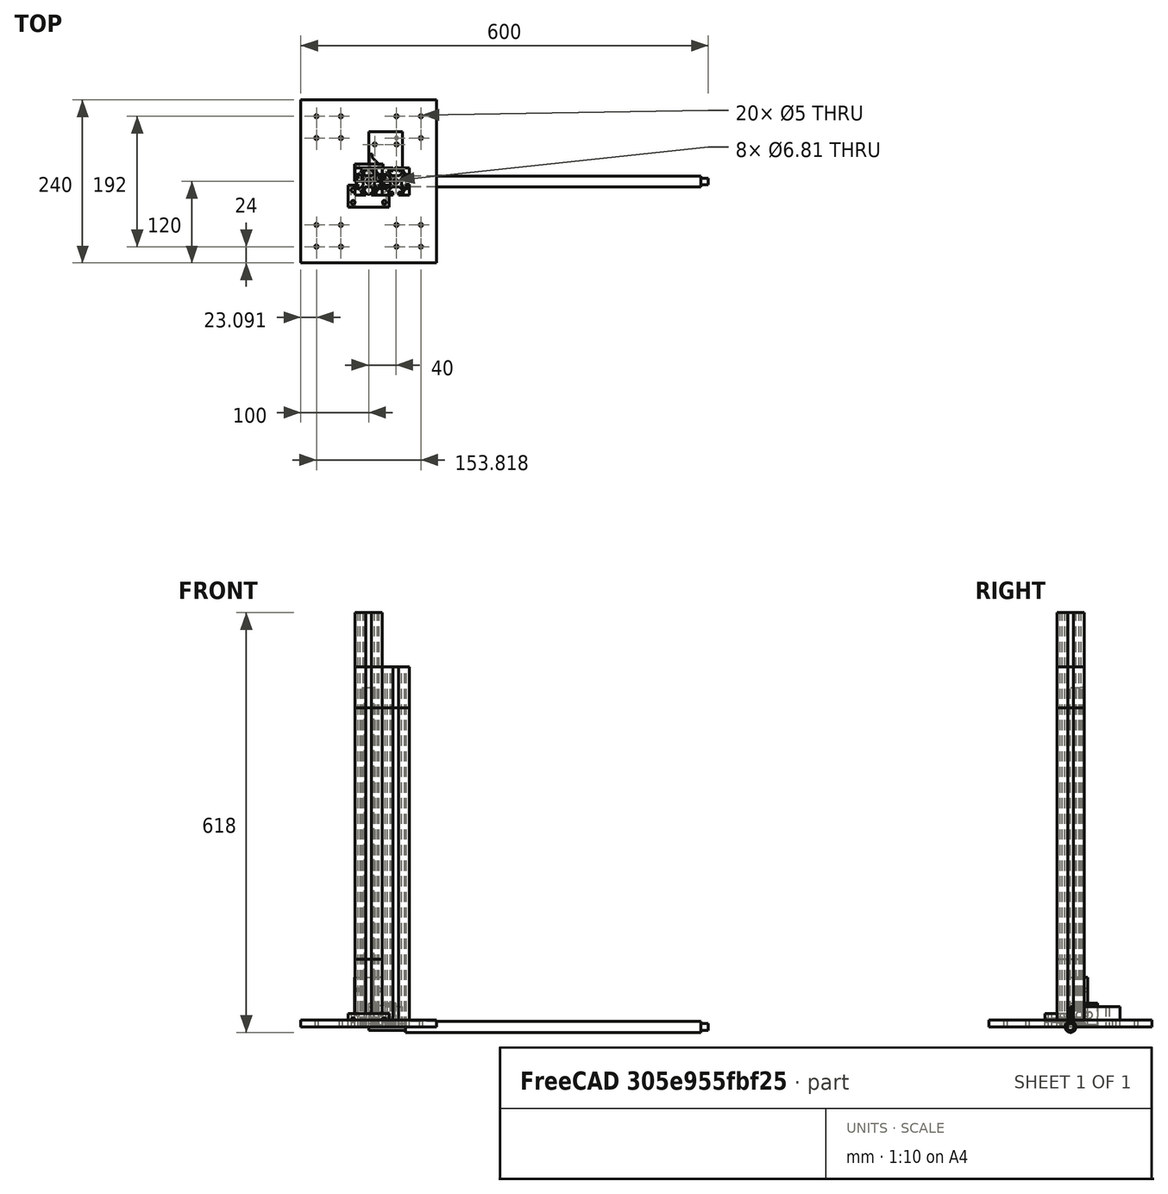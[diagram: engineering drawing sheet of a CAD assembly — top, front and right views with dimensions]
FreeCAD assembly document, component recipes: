
FREECAD ASSEMBLY — COMPONENT RECIPES ("cnc")

This assembly document has 70 components, labeled P0..P69 below (a component is one placed body or linked part). 34 of them carry a construction recipe — the FreeCAD feature program that regenerates the part from scratch, quoted from this document or its linked companion documents; the rest are supplied as boundary geometry only. No exploded tour is included for this assembly.
COMPONENT P0 — recipe-attached ("BF013", modeled in this document).
Construction recipe (the document's own serialized feature program — sketch geometry with constraints, then the solid features built on it; lengths are millimeters unless a unit is written):

FEATURE [Sketcher::SketchObject] Sketch028
  ArcFitTolerance = 1e-06
  AttachmentSupport = -> [XY_Plane023]
  FullyConstrained = true
  MakeInternals = false
  MapMode = 5
  sketch-geometry (17):
    g0: LineSegment StartX=30 StartY=-37.75 StartZ=0 EndX=-30 EndY=-37.75 EndZ=0
    g1: LineSegment StartX=-30 StartY=-37.75 StartZ=0 EndX=-30 EndY=-5.25 EndZ=0
    g2: LineSegment StartX=-30 StartY=-5.25 StartZ=0 EndX=-18 EndY=-5.25 EndZ=0
    g3: LineSegment StartX=-18 StartY=-5.25 StartZ=0 EndX=-18 EndY=5.25 EndZ=0
    g4: LineSegment StartX=-18 StartY=5.25 StartZ=0 EndX=18 EndY=5.25 EndZ=0
    g5: LineSegment StartX=18 StartY=5.25 StartZ=0 EndX=18 EndY=-5.25 EndZ=0
    g6: LineSegment StartX=18 StartY=-5.25 StartZ=0 EndX=30 EndY=-5.25 EndZ=0
    g7: LineSegment StartX=30 StartY=-5.25 StartZ=0 EndX=30 EndY=-37.75 EndZ=0
    g8: Circle CenterX=-23 CenterY=-30.75 CenterZ=0 NormalX=0 NormalY=0 NormalZ=1 AngleXU=0 Radius=2.75
    g9: Circle CenterX=-23 CenterY=-12.75 CenterZ=0 NormalX=0 NormalY=0 NormalZ=1 AngleXU=0 Radius=2.75
    g10: Circle CenterX=23 CenterY=-12.75 CenterZ=0 NormalX=0 NormalY=0 NormalZ=1 AngleXU=0 Radius=2.75
    g11: Circle CenterX=23 CenterY=-30.75 CenterZ=0 NormalX=0 NormalY=0 NormalZ=1 AngleXU=0 Radius=2.75
    g12: LineSegment [constr] StartX=-23 StartY=-12.75 StartZ=0 EndX=23 EndY=-12.75 EndZ=0
    g13: LineSegment [constr] StartX=-23 StartY=-30.75 StartZ=0 EndX=23 EndY=-30.75 EndZ=0
    g14: LineSegment [constr] StartX=-23 StartY=-12.75 StartZ=0 EndX=-23 EndY=-30.75 EndZ=0
    g15: LineSegment [constr] StartX=23 StartY=-12.75 StartZ=0 EndX=23 EndY=-30.75 EndZ=0
    g16: Circle CenterX=0 CenterY=-12.75 CenterZ=0 NormalX=0 NormalY=0 NormalZ=1 AngleXU=0 Radius=6
  constraints (41):
    c: Horizontal(g0)
    c: Coincident(g1,g0)
    c: Coincident(g2,g1)
    c: Coincident(g3,g2)
    c: Vertical(g3)
    c: Coincident(g4,g3)
    c: Coincident(g5,g4)
    c: Coincident(g7,g0)
    c: Coincident(g6,g7)
    c: Coincident(g5,g6)
    c: Horizontal(g6)
    c: Vertical(g1)
    c: Vertical(g7)
    c: Tangent(g2,g6)
    c: Equal(g2,g6)
    c: DistanceX(g0,g0) = 60
    c: Symmetric(g3,g4,g-2)
    c: Symmetric(g5,g4,g-1)
    c: DistanceY(g7,g7) = 32.5
    c: Distance(g0,g4) = 43
    c: DistanceX(g2,g2) = 12
    c: Equal(g11,g10)
    c: Equal(g10,g9)
    c: Equal(g9,g8)
    c: Diameter(g8) = 5.5
    c: Distance(g8,g0) = 7
    c: DistanceY(g8,g9) = 18
    c: Coincident(g12,g9)
    c: Coincident(g12,g10)
    c: Coincident(g13,g8)
    c: Coincident(g13,g11)
    c: Symmetric(g9,g10,g-2)
    c: Symmetric(g8,g11,g-2)
    c: Coincident(g14,g9)
    c: Coincident(g14,g8)
    c: Vertical(g14)
    c: Coincident(g15,g10)
    c: Coincident(g15,g11)
    c: Distance(g15,g14) = 46
    c: Symmetric(g12,g12,g16)
    c: Diameter(g16) = 12
FEATURE [PartDesign::Pad] Pad018
  Direction = (0,0,1)
  Length = 20
  Length2 = 10
  Profile = -> Sketch028
  ReferenceAxis = -> Sketch028 [N_Axis]
  Refine = true
  Suppressed = false
  Type = 0
FEATURE [Sketcher::SketchObject] Sketch029
  ArcFitTolerance = 1e-06
  AttachmentSupport = -> [Pad018]
  FullyConstrained = true
  MakeInternals = false
  MapMode = 5
  Placement = pos=(0,-5.25,0) rot=(0,0.707107,0.707107;3.14159rad)
  sketch-geometry (2):
    g0: Circle CenterX=-23 CenterY=10 CenterZ=0 NormalX=0 NormalY=0 NormalZ=1 AngleXU=0 Radius=3.3
    g1: Circle CenterX=23 CenterY=10 CenterZ=0 NormalX=0 NormalY=0 NormalZ=1 AngleXU=0 Radius=3.3
  constraints (5):
    c: Equal(g1,g0)
    c: Diameter(g0) = 6.6
    c: Symmetric(g0,g1,g-2)
    c: Distance(g0,g-1) = 10
    c: DistanceX(g0,g1) = 46
FEATURE [PartDesign::Pocket] Pocket002
  BaseFeature = -> Pad018
  Direction = (0,-1,2e-16)
  Length = 5
  Length2 = 5
  Profile = -> Sketch029
  ReferenceAxis = -> Sketch029 [N_Axis]
  Refine = true
  Suppressed = false
  Type = 1
FEATURE [PartDesign::Body] Body018  label="BF12"
  AllowCompound = false
  Group = -> [Sketch028,Pad018,Sketch029,Pocket002]
  Origin = -> Origin023
  Tip = -> Pocket002
COMPONENT P1 — recipe-attached ("HGR20 carriage006", modeled in this document).
Construction recipe (the document's own serialized feature program — sketch geometry with constraints, then the solid features built on it; lengths are millimeters unless a unit is written):

FEATURE [Sketcher::SketchObject] Sketch011
  ArcFitTolerance = 1e-06
  AttachmentSupport = -> [XY_Plane009]
  FullyConstrained = true
  MakeInternals = false
  MapMode = 5
  sketch-geometry (14):
    g0: LineSegment StartX=10 StartY=0 StartZ=0 EndX=10 EndY=3.9 EndZ=0
    g1: LineSegment StartX=-10 StartY=0 StartZ=0 EndX=-10 EndY=3.9 EndZ=0
    g2: LineSegment StartX=-10 StartY=9.9 StartZ=0 EndX=-10 EndY=13.1218 EndZ=0
    g3: LineSegment StartX=-10 StartY=13.1218 StartZ=0 EndX=-7.72183 EndY=15.4 EndZ=0
    g4: LineSegment StartX=-7.72183 StartY=15.4 StartZ=0 EndX=7.72183 EndY=15.4 EndZ=0
    g5: LineSegment StartX=7.72183 StartY=15.4 StartZ=0 EndX=10 EndY=13.1218 EndZ=0
    g6: LineSegment StartX=10 StartY=13.1218 StartZ=0 EndX=10 EndY=9.9 EndZ=0
    g7: ArcOfCircle CenterX=-10 CenterY=6.9 CenterZ=0 NormalX=0 NormalY=0 NormalZ=1 AngleXU=0 Radius=3 StartAngle=4.71239 EndAngle=7.85398
    g8: ArcOfCircle CenterX=10 CenterY=6.9 CenterZ=0 NormalX=0 NormalY=0 NormalZ=1 AngleXU=0 Radius=3 StartAngle=1.5708 EndAngle=4.71238
    g9: LineSegment StartX=-21 StartY=0 StartZ=0 EndX=-21 EndY=25.4 EndZ=0
    g10: LineSegment StartX=-21 StartY=25.4 StartZ=0 EndX=21 EndY=25.4 EndZ=0
    g11: LineSegment StartX=21 StartY=25.4 StartZ=0 EndX=21 EndY=0 EndZ=0
    g12: LineSegment StartX=21 StartY=0 StartZ=0 EndX=10 EndY=0 EndZ=0
    g13: LineSegment StartX=-21 StartY=0 StartZ=0 EndX=-10 EndY=0 EndZ=0
  constraints (42):
    c: Coincident(g3,g2)
    c: Coincident(g4,g3)
    c: Horizontal(g4)
    c: Coincident(g5,g4)
    c: Coincident(g6,g5)
    c: Vertical(g6)
    c: Coincident(g7,g2)
    c: Coincident(g7,g1)
    c: Coincident(g8,g0)
    c: Coincident(g8,g6)
    c: Equal(g7,g8)
    c: Equal(g0,g1)
    c: Equal(g2,g6)
    c: Equal(g5,g3)
    c: Distance(g1,g0) = 20
    c: Symmetric(g1,g0,g-2)
    c: Vertical(g1)
    c: Vertical(g0)
    c: Tangent(g2,g1)
    c: PointOnObject(g6,g0)
    c: Radius(g7) = 3
    c: Angle(g3,g2) = 0.785398
    c: Angle(g5,g6) = 2.35619
    c: PointOnObject(g7,g2)
    c: Distance(g7,g4) = 8.5
    c: Equal(g3,g2)
    c: Vertical(g9)
    c: Coincident(g10,g9)
    c: Horizontal(g10)
    c: Coincident(g11,g10)
    c: PointOnObject(g11,g-1)
    c: Vertical(g11)
    c: Coincident(g12,g11)
    c: DistanceX(g10,g10) = 42
    c: Coincident(g12,g0)
    c: DistanceY(g9,g9) = 25.4
    c: Coincident(g13,g9)
    c: Coincident(g13,g1)
    c: Horizontal(g13)
    c: Equal(g13,g12)
    c: Horizontal(g12)
    c: Distance(g10,g4) = 10
FEATURE [PartDesign::Pad] Pad007
  Direction = (0,0,1)
  Length = 73
  Length2 = 10
  Profile = -> Sketch011
  ReferenceAxis = -> Sketch011 [N_Axis]
  Refine = true
  Suppressed = false
  Type = 0
FEATURE [Sketcher::SketchObject] Sketch012
  ArcFitTolerance = 1e-06
  AttachmentSupport = -> [Pad007]
  FullyConstrained = true
  MakeInternals = false
  MapMode = 5
  Placement = pos=(0,25.4,0) rot=(0,0.707107,0.707107;3.14159rad)
  sketch-geometry (8):
    g0: Circle CenterX=-16 CenterY=54.5 CenterZ=0 NormalX=0 NormalY=0 NormalZ=1 AngleXU=0 Radius=2.5
    g1: Circle CenterX=16 CenterY=54.5 CenterZ=0 NormalX=0 NormalY=0 NormalZ=1 AngleXU=0 Radius=2.5
    g2: Circle CenterX=-16 CenterY=18.5 CenterZ=0 NormalX=0 NormalY=0 NormalZ=1 AngleXU=0 Radius=2.5
    g3: Circle CenterX=16 CenterY=18.5 CenterZ=0 NormalX=0 NormalY=0 NormalZ=1 AngleXU=0 Radius=2.5
    g4: LineSegment [constr] StartX=-16 StartY=54.5 StartZ=0 EndX=16 EndY=54.5 EndZ=0
    g5: LineSegment [constr] StartX=-16 StartY=18.5 StartZ=0 EndX=16 EndY=18.5 EndZ=0
    g6: LineSegment [constr] StartX=16 StartY=54.5 StartZ=0 EndX=16 EndY=18.5 EndZ=0
    g7: LineSegment [constr] StartX=-16 StartY=54.5 StartZ=0 EndX=-16 EndY=18.5 EndZ=0
  constraints (19):
    c: Equal(g1,g0)
    c: Equal(g0,g3)
    c: Equal(g3,g2)
    c: Diameter(g0) = 5
    c: DistanceY(g3,g1) = 36
    c: Coincident(g4,g0)
    c: Coincident(g4,g1)
    c: Coincident(g5,g2)
    c: Coincident(g5,g3)
    c: Horizontal(g5)
    c: Coincident(g6,g1)
    c: Coincident(g6,g3)
    c: Vertical(g6)
    c: Coincident(g7,g0)
    c: Coincident(g7,g2)
    c: Vertical(g7)
    c: DistanceX(g4,g4) = 32
    c: Symmetric(g0,g1,g-2)
    c: Distance(g-1,g5) = 18.5
FEATURE [PartDesign::Pocket] Pocket
  BaseFeature = -> Pad007
  Direction = (0,-1,2e-16)
  Length = 5
  Length2 = 5
  Profile = -> Sketch012
  ReferenceAxis = -> Sketch012 [N_Axis]
  Refine = true
  Suppressed = false
  Type = 0
FEATURE [PartDesign::Body] Body007  label="HGR20 carriage"
  AllowCompound = false
  Group = -> [Sketch011,Pad007,Sketch012,Pocket]
  Origin = -> Origin009
  Tip = -> Pocket
COMPONENT P2 — same part as P1; its construction recipe is shown at P1.
COMPONENT P3 — same part as P1; its construction recipe is shown at P1.
COMPONENT P4 — same part as P1; its construction recipe is shown at P1.
COMPONENT P5 — recipe-attached ("HGR20x502", modeled in this document).
Construction recipe (the document's own serialized feature program — sketch geometry with constraints, then the solid features built on it; lengths are millimeters unless a unit is written):

FEATURE [Sketcher::SketchObject] Sketch010
  ArcFitTolerance = 1e-06
  AttachmentSupport = -> [XY_Plane]
  FullyConstrained = true
  MakeInternals = false
  MapMode = 5
  sketch-geometry (10):
    g0: LineSegment StartX=-10 StartY=0 StartZ=0 EndX=10 EndY=0 EndZ=0
    g1: LineSegment StartX=10 StartY=0 StartZ=0 EndX=10 EndY=8.5 EndZ=0
    g2: LineSegment StartX=-10 StartY=0 StartZ=0 EndX=-10 EndY=8.5 EndZ=0
    g3: LineSegment StartX=-10 StartY=14.5 StartZ=0 EndX=-10 EndY=17.7218 EndZ=0
    g4: LineSegment StartX=-10 StartY=17.7218 StartZ=0 EndX=-7.72183 EndY=20 EndZ=0
    g5: LineSegment StartX=-7.72183 StartY=20 StartZ=0 EndX=7.72183 EndY=20 EndZ=0
    g6: LineSegment StartX=7.72183 StartY=20 StartZ=0 EndX=10 EndY=17.7218 EndZ=0
    g7: LineSegment StartX=10 StartY=17.7218 StartZ=0 EndX=10 EndY=14.5 EndZ=0
    g8: ArcOfCircle CenterX=-10 CenterY=11.5 CenterZ=0 NormalX=0 NormalY=0 NormalZ=1 AngleXU=0 Radius=3 StartAngle=4.71239 EndAngle=7.85398
    g9: ArcOfCircle CenterX=9.99998 CenterY=11.5 CenterZ=0 NormalX=0 NormalY=0 NormalZ=1 AngleXU=0 Radius=3 StartAngle=1.57079 EndAngle=4.7124
  constraints (30):
    c: Coincident(g1,g0)
    c: Coincident(g2,g0)
    c: Coincident(g4,g3)
    c: Coincident(g5,g4)
    c: Horizontal(g5)
    c: Coincident(g6,g5)
    c: Coincident(g7,g6)
    c: Vertical(g7)
    c: Coincident(g8,g3)
    c: Coincident(g8,g2)
    c: Coincident(g9,g1)
    c: Coincident(g9,g7)
    c: Equal(g8,g9)
    c: Equal(g1,g2)
    c: Equal(g3,g7)
    c: Equal(g6,g4)
    c: Distance(g0,g0) = 20
    c: Symmetric(g0,g0,g-2)
    c: Vertical(g2)
    c: Vertical(g1)
    c: Tangent(g3,g2)
    c: PointOnObject(g7,g1)
    c: Radius(g8) = 3
    c: Angle(g4,g3) = 0.785398
    c: Angle(g6,g7) = 2.35619
    c: Distance(g0,g5) = 20
    c: PointOnObject(g8,g3)
    c: Distance(g8,g5) = 8.5
    c: PointOnObject(g-1,g0)
    c: Equal(g4,g3)
FEATURE [PartDesign::Pad] Pad006
  Direction = (0,0,1)
  Length = 500
  Length2 = 10
  Profile = -> Sketch010
  ReferenceAxis = -> Sketch010 [N_Axis]
  Refine = true
  Suppressed = false
  Type = 0
FEATURE [PartDesign::Body] Body  label="HGR20x500"
  AllowCompound = false
  Group = -> [Sketch010,Pad006]
  Origin = -> Origin
  Tip = -> Pad006
COMPONENT P6 — same part as P5; its construction recipe is shown at P5.
COMPONENT P7 — recipe-attached ("XY gantry plate003", modeled in this document).
Construction recipe (the document's own serialized feature program — sketch geometry with constraints, then the solid features built on it; lengths are millimeters unless a unit is written):

FEATURE [Sketcher::SketchObject] Sketch013
  ArcFitTolerance = 1e-06
  AttachmentSupport = -> [XY_Plane010]
  FullyConstrained = false
  MakeInternals = false
  MapMode = 5
  sketch-geometry (28):
    g0: LineSegment StartX=-100 StartY=120 StartZ=0 EndX=-100 EndY=-120 EndZ=0
    g1: LineSegment StartX=-100 StartY=-120 StartZ=0 EndX=100 EndY=-120 EndZ=0
    g2: LineSegment StartX=100 StartY=-120 StartZ=0 EndX=100 EndY=120 EndZ=0
    g3: LineSegment StartX=100 StartY=120 StartZ=0 EndX=-100 EndY=120 EndZ=0
    g4: Circle CenterX=-76.9092 CenterY=96 CenterZ=0 NormalX=0 NormalY=0 NormalZ=1 AngleXU=0 Radius=2.5
    g5: Circle CenterX=-40.9092 CenterY=96 CenterZ=0 NormalX=0 NormalY=0 NormalZ=1 AngleXU=0 Radius=2.5
    g6: Circle CenterX=-76.9092 CenterY=64 CenterZ=0 NormalX=0 NormalY=0 NormalZ=1 AngleXU=0 Radius=2.5
    g7: Circle CenterX=-40.9092 CenterY=64 CenterZ=0 NormalX=0 NormalY=0 NormalZ=1 AngleXU=0 Radius=2.5
    g8: Circle CenterX=-76.9092 CenterY=-64 CenterZ=0 NormalX=0 NormalY=0 NormalZ=1 AngleXU=0 Radius=2.5
    g9: Circle CenterX=-40.9092 CenterY=-64 CenterZ=0 NormalX=0 NormalY=0 NormalZ=1 AngleXU=0 Radius=2.5
    g10: Circle CenterX=-76.9092 CenterY=-96 CenterZ=0 NormalX=0 NormalY=0 NormalZ=1 AngleXU=0 Radius=2.5
    g11: Circle CenterX=-40.9092 CenterY=-96 CenterZ=0 NormalX=0 NormalY=0 NormalZ=1 AngleXU=0 Radius=2.5
    g12: Circle CenterX=40.9092 CenterY=96 CenterZ=0 NormalX=0 NormalY=0 NormalZ=1 AngleXU=0 Radius=2.5
    g13: Circle CenterX=76.9092 CenterY=96 CenterZ=0 NormalX=0 NormalY=0 NormalZ=1 AngleXU=0 Radius=2.5
    g14: Circle CenterX=40.9092 CenterY=64 CenterZ=0 NormalX=0 NormalY=0 NormalZ=1 AngleXU=0 Radius=2.5
    g15: Circle CenterX=76.9092 CenterY=64 CenterZ=0 NormalX=0 NormalY=0 NormalZ=1 AngleXU=0 Radius=2.5
    g16: Circle CenterX=40.9092 CenterY=-64 CenterZ=0 NormalX=0 NormalY=0 NormalZ=1 AngleXU=0 Radius=2.5
    g17: Circle CenterX=76.9092 CenterY=-64 CenterZ=0 NormalX=0 NormalY=0 NormalZ=1 AngleXU=0 Radius=2.5
    g18: Circle CenterX=40.9092 CenterY=-96 CenterZ=0 NormalX=0 NormalY=0 NormalZ=1 AngleXU=0 Radius=2.5
    g19: Circle CenterX=76.9092 CenterY=-96 CenterZ=0 NormalX=0 NormalY=0 NormalZ=1 AngleXU=0 Radius=2.5
    g20: LineSegment [constr] StartX=-76.9092 StartY=96 StartZ=0 EndX=76.9092 EndY=96 EndZ=0
    g21: LineSegment [constr] StartX=76.9092 StartY=96 StartZ=0 EndX=76.9092 EndY=-96 EndZ=0
    g22: LineSegment [constr] StartX=76.9092 StartY=-96 StartZ=0 EndX=-76.9092 EndY=-96 EndZ=0
    g23: LineSegment [constr] StartX=-76.9092 StartY=-96 StartZ=0 EndX=-76.9092 EndY=96 EndZ=0
    g24: LineSegment [constr] StartX=-76.9092 StartY=64 StartZ=0 EndX=76.9092 EndY=64 EndZ=0
    g25: LineSegment [constr] StartX=-76.9092 StartY=-64 StartZ=0 EndX=76.9092 EndY=-64 EndZ=0
    g26: LineSegment [constr] StartX=40.9092 StartY=96 StartZ=0 EndX=40.9092 EndY=-96 EndZ=0
    g27: LineSegment [constr] StartX=-40.9092 StartY=-96 StartZ=0 EndX=-40.9092 EndY=96 EndZ=0
  constraints (71):
    c: Coincident(g0,g1)
    c: Coincident(g1,g2)
    c: Coincident(g2,g3)
    c: Coincident(g3,g0)
    c: Vertical(g2)
    c: Horizontal(g1)
    c: Equal(g17,g16)
    c: Equal(g16,g18)
    c: Equal(g18,g19)
    c: Equal(g19,g14)
    c: Equal(g14,g15)
    c: Equal(g15,g13)
    c: Equal(g13,g12)
    c: Equal(g12,g5)
    c: Equal(g5,g4)
    c: Equal(g4,g6)
    c: Equal(g6,g7)
    c: Equal(g7,g8)
    c: Equal(g8,g9)
    c: Equal(g9,g11)
    c: Equal(g11,g10)
    c: Diameter(g4) = 5
    c: Coincident(g20,g4)
    c: Coincident(g20,g13)
    c: Coincident(g21,g13)
    c: Coincident(g21,g19)
    c: Coincident(g22,g19)
    c: Coincident(g22,g10)
    c: Coincident(g23,g10)
    c: Coincident(g23,g4)
    c: PointOnObject(g6,g23)
    c: PointOnObject(g8,g23)
    c: PointOnObject(g11,g22)
    c: PointOnObject(g18,g22)
    c: PointOnObject(g17,g21)
    c: PointOnObject(g15,g21)
    c: PointOnObject(g12,g20)
    c: PointOnObject(g5,g20)
    c: Vertical(g21)
    c: Horizontal(g22)
    c: Coincident(g24,g6)
    c: Horizontal(g24)
    c: Coincident(g25,g8)
    c: Coincident(g25,g17)
    c: Coincident(g26,g12)
    c: Coincident(g26,g18)
    c: Vertical(g26)
    c: Coincident(g27,g11)
    c: Coincident(g27,g5)
    c: Vertical(g27)
    c: Horizontal(g25)
    c: PointOnObject(g9,g25)
    c: PointOnObject(g9,g27)
    c: PointOnObject(g7,g24)
    c: PointOnObject(g7,g27)
    c: PointOnObject(g14,g24)
    c: PointOnObject(g14,g26)
    c: Coincident(g15,g24)
    c: PointOnObject(g16,g26)
    c: PointOnObject(g16,g25)
    c: Distance(g24,g20) = 32
    c: Distance(g25,g22) = 32
    c: Distance(g27,g23) = 36
    c: Distance(g21,g26) = 36
    c: Distance(g1,g3) = 240
    c: Distance(g2,g0) = 200
    c: Symmetric(g5,g12,g-2)
    c: Symmetric(g10,g4,g-1)
    c: Symmetric(g0,g0,g-1)
    c: Symmetric(g0,g2,g-2)
    c: DistanceY(g9,g5) = 160
FEATURE [PartDesign::Pad] Pad008
  Direction = (0,0,1)
  Length = 10
  Length2 = 10
  Profile = -> Sketch013
  ReferenceAxis = -> Sketch013 [N_Axis]
  Refine = true
  Suppressed = false
  Type = 0
FEATURE [PartDesign::Body] Body008  label="XY gantry plate"
  AllowCompound = false
  Group = -> [Sketch013,Pad008]
  Origin = -> Origin010
  Tip = -> Pad008
COMPONENT P8 — recipe-attached ("4040 extrusion @ 627", modeled in this document).
Construction recipe (the document's own serialized feature program — sketch geometry with constraints, then the solid features built on it; lengths are millimeters unless a unit is written):

FEATURE [Sketcher::SketchObject] Sketch006
  ArcFitTolerance = 1e-06
  AttachmentSupport = -> [XY_Plane008]
  FullyConstrained = true
  MakeInternals = false
  MapMode = 5
  sketch-geometry (37):
    g0: LineSegment StartX=-20 StartY=4.065 StartZ=0 EndX=-20 EndY=20 EndZ=0
    g1: LineSegment StartX=-20 StartY=20 StartZ=0 EndX=-4.065 EndY=20 EndZ=0
    g2: LineSegment StartX=-4.065 StartY=20 StartZ=0 EndX=-4.065 EndY=15.68 EndZ=0
    g3: LineSegment StartX=-4.065 StartY=15.68 StartZ=0 EndX=-12.6253 EndY=15.68 EndZ=0
    g4: LineSegment StartX=-12.6253 StartY=15.68 StartZ=0 EndX=-5.22957 EndY=8.28427 EndZ=0
    g5: LineSegment StartX=-5.22957 StartY=8.28427 StartZ=0 EndX=5.22957 EndY=8.28427 EndZ=0
    g6: LineSegment StartX=5.22957 StartY=8.28427 StartZ=0 EndX=12.6253 EndY=15.68 EndZ=0
    g7: LineSegment StartX=12.6253 StartY=15.68 StartZ=0 EndX=4.065 EndY=15.68 EndZ=0
    g8: LineSegment StartX=4.065 StartY=15.68 StartZ=0 EndX=4.065 EndY=20 EndZ=0
    g9: LineSegment StartX=4.065 StartY=20 StartZ=0 EndX=20 EndY=20 EndZ=0
    g10: LineSegment StartX=20 StartY=20 StartZ=0 EndX=20 EndY=4.065 EndZ=0
    g11: LineSegment StartX=20 StartY=4.065 StartZ=0 EndX=15.68 EndY=4.065 EndZ=0
    g12: LineSegment StartX=15.68 StartY=4.065 StartZ=0 EndX=15.68 EndY=12.6253 EndZ=0
    g13: LineSegment StartX=15.68 StartY=12.6253 StartZ=0 EndX=8.28427 EndY=5.22957 EndZ=0
    g14: LineSegment StartX=8.28427 StartY=5.22957 StartZ=0 EndX=8.28427 EndY=-5.22957 EndZ=0
    g15: LineSegment StartX=8.28427 StartY=-5.22957 StartZ=0 EndX=15.68 EndY=-12.6253 EndZ=0
    g16: LineSegment StartX=15.68 StartY=-12.6253 StartZ=0 EndX=15.68 EndY=-4.065 EndZ=0
    g17: LineSegment StartX=15.68 StartY=-4.065 StartZ=0 EndX=20 EndY=-4.065 EndZ=0
    g18: LineSegment StartX=20 StartY=-4.065 StartZ=0 EndX=20 EndY=-20 EndZ=0
    g19: LineSegment StartX=20 StartY=-20 StartZ=0 EndX=4.065 EndY=-20 EndZ=0
    g20: LineSegment StartX=4.065 StartY=-20 StartZ=0 EndX=4.065 EndY=-15.68 EndZ=0
    g21: LineSegment StartX=4.065 StartY=-15.68 StartZ=0 EndX=12.6253 EndY=-15.68 EndZ=0
    g22: LineSegment StartX=12.6253 StartY=-15.68 StartZ=0 EndX=5.22957 EndY=-8.28427 EndZ=0
    g23: LineSegment StartX=5.22957 StartY=-8.28427 StartZ=0 EndX=-5.22957 EndY=-8.28427 EndZ=0
    g24: LineSegment StartX=-5.22957 StartY=-8.28427 StartZ=0 EndX=-12.6253 EndY=-15.68 EndZ=0
    g25: LineSegment StartX=-12.6253 StartY=-15.68 StartZ=0 EndX=-4.065 EndY=-15.68 EndZ=0
    g26: LineSegment StartX=-4.065 StartY=-15.68 StartZ=0 EndX=-4.065 EndY=-20 EndZ=0
    g27: LineSegment StartX=-4.065 StartY=-20 StartZ=0 EndX=-20 EndY=-20 EndZ=0
    g28: LineSegment StartX=-20 StartY=-20 StartZ=0 EndX=-20 EndY=-4.065 EndZ=0
    g29: LineSegment StartX=-20 StartY=-4.065 StartZ=0 EndX=-15.68 EndY=-4.065 EndZ=0
    g30: LineSegment StartX=-15.68 StartY=-4.065 StartZ=0 EndX=-15.68 EndY=-12.6253 EndZ=0
    g31: LineSegment StartX=-15.68 StartY=-12.6253 StartZ=0 EndX=-8.28427 EndY=-5.22957 EndZ=0
    g32: LineSegment StartX=-8.28427 StartY=-5.22957 StartZ=0 EndX=-8.28427 EndY=5.22957 EndZ=0
    g33: LineSegment StartX=-8.28427 StartY=5.22957 StartZ=0 EndX=-15.68 EndY=12.6253 EndZ=0
    g34: LineSegment StartX=-15.68 StartY=12.6253 StartZ=0 EndX=-15.68 EndY=4.065 EndZ=0
    g35: LineSegment StartX=-15.68 StartY=4.065 StartZ=0 EndX=-20 EndY=4.065 EndZ=0
    g36: Circle CenterX=0 CenterY=0 CenterZ=0 NormalX=0 NormalY=0 NormalZ=1 AngleXU=0 Radius=3.405
  constraints (100):
    c: Coincident(g24,g23)
    c: Coincident(g32,g31)
    c: Coincident(g30,g31)
    c: Coincident(g25,g24)
    c: Coincident(g25,g26)
    c: Coincident(g20,g21)
    c: Coincident(g19,g20)
    c: Coincident(g26,g27)
    c: Coincident(g28,g27)
    c: Coincident(g21,g22)
    c: Coincident(g19,g18)
    c: Coincident(g16,g15)
    c: Coincident(g14,g15)
    c: Coincident(g23,g22)
    c: Coincident(g16,g17)
    c: Coincident(g18,g17)
    c: Coincident(g12,g11)
    c: Coincident(g11,g10)
    c: Coincident(g10,g9)
    c: Coincident(g13,g12)
    c: Coincident(g13,g14)
    c: Coincident(g6,g5)
    c: Coincident(g7,g6)
    c: Coincident(g8,g7)
    c: Coincident(g9,g8)
    c: Coincident(g2,g1)
    c: Coincident(g2,g3)
    c: Coincident(g4,g3)
    c: Coincident(g34,g33)
    c: Coincident(g5,g4)
    c: Coincident(g33,g32)
    c: Coincident(g35,g34)
    c: Coincident(g35,g0)
    c: Coincident(g1,g0)
    c: Coincident(g30,g29)
    c: Coincident(g29,g28)
    c: Distance(g10,g0) = 40
    c: Distance(g27,g1) = 40
    c: Tangent(g1,g9)
    c: Tangent(g27,g19)
    c: Tangent(g0,g28)
    c: Tangent(g10,g18)
    c: Horizontal(g1)
    c: Vertical(g0)
    c: Equal(g2,g8)
    c: Equal(g8,g35)
    c: Equal(g35,g29)
    c: Equal(g29,g26)
    c: Equal(g26,g20)
    c: Equal(g20,g17)
    c: Equal(g17,g11)
    c: Vertical(g34)
    c: Vertical(g30)
    c: Vertical(g16)
    c: Vertical(g18)
    c: Vertical(g12)
    c: Vertical(g8)
    c: Vertical(g2)
    c: Vertical(g14)
    c: Vertical(g32)
    c: Horizontal(g35)
    c: Horizontal(g29)
    c: Horizontal(g23)
    c: Horizontal(g19)
    c: Horizontal(g25)
    c: Horizontal(g21)
    c: Horizontal(g7)
    c: Horizontal(g3)
    c: Parallel(g4,g33)
    c: Parallel(g33,g15)
    c: Parallel(g15,g22)
    c: Parallel(g6,g13)
    c: Parallel(g13,g24)
    c: Parallel(g24,g31)
    c: Equal(g23,g24)
    c: Equal(g24,g31)
    c: Equal(g4,g33)
    c: Equal(g6,g13)
    c: Equal(g15,g22)
    c: Angle(g25,g24) = 0.785398
    c: Distance(g8,g2) = 8.13
    c: Distance(g29,g35) = 8.13
    c: Tangent(g35,g11)
    c: Tangent(g17,g29)
    c: Tangent(g2,g26)
    c: Tangent(g8,g20)
    c: Distance(g22,g15) = 4.32
    c: Distance(g13,g6) = 4.32
    c: Distance(g33,g4) = 4.32
    c: Distance(g24,g31) = 4.32
    c: Equal(g32,g14)
    c: Equal(g5,g23)
    c: Equal(g25,g21)
    c: Equal(g34,g30)
    c: Distance(g35,g35) = 4.32
    c: Symmetric(g5,g22,g-1)
    c: Symmetric(g4,g5,g-2)
    c: Equal(g5,g32)
    c: Coincident(g36,g-1)
    c: Diameter(g36) = 6.81
FEATURE [PartDesign::Pad] Pad005
  Direction = (0,0,1)
  Length = 100
  Length2 = 10
  Profile = -> Sketch006
  ReferenceAxis = -> Sketch006 [N_Axis]
  Refine = true
  Suppressed = false
  Type = 0
FEATURE [PartDesign::Body] Body006  label="4040 extrusion @ 100"
  AllowCompound = false
  Group = -> [Sketch006,Pad005]
  Origin = -> Origin008
  Tip = -> Pad005
COMPONENT P9 — recipe-attached ("4040 extrusion @ 619", modeled in this document).
Construction recipe (the document's own serialized feature program — sketch geometry with constraints, then the solid features built on it; lengths are millimeters unless a unit is written):

FEATURE [Sketcher::SketchObject] Sketch003
  ArcFitTolerance = 1e-06
  AttachmentSupport = -> [XY_Plane005]
  FullyConstrained = true
  MakeInternals = false
  MapMode = 5
  sketch-geometry (37):
    g0: LineSegment StartX=-20 StartY=4.065 StartZ=0 EndX=-20 EndY=20 EndZ=0
    g1: LineSegment StartX=-20 StartY=20 StartZ=0 EndX=-4.065 EndY=20 EndZ=0
    g2: LineSegment StartX=-4.065 StartY=20 StartZ=0 EndX=-4.065 EndY=15.68 EndZ=0
    g3: LineSegment StartX=-4.065 StartY=15.68 StartZ=0 EndX=-12.6253 EndY=15.68 EndZ=0
    g4: LineSegment StartX=-12.6253 StartY=15.68 StartZ=0 EndX=-5.22957 EndY=8.28427 EndZ=0
    g5: LineSegment StartX=-5.22957 StartY=8.28427 StartZ=0 EndX=5.22957 EndY=8.28427 EndZ=0
    g6: LineSegment StartX=5.22957 StartY=8.28427 StartZ=0 EndX=12.6253 EndY=15.68 EndZ=0
    g7: LineSegment StartX=12.6253 StartY=15.68 StartZ=0 EndX=4.065 EndY=15.68 EndZ=0
    g8: LineSegment StartX=4.065 StartY=15.68 StartZ=0 EndX=4.065 EndY=20 EndZ=0
    g9: LineSegment StartX=4.065 StartY=20 StartZ=0 EndX=20 EndY=20 EndZ=0
    g10: LineSegment StartX=20 StartY=20 StartZ=0 EndX=20 EndY=4.065 EndZ=0
    g11: LineSegment StartX=20 StartY=4.065 StartZ=0 EndX=15.68 EndY=4.065 EndZ=0
    g12: LineSegment StartX=15.68 StartY=4.065 StartZ=0 EndX=15.68 EndY=12.6253 EndZ=0
    g13: LineSegment StartX=15.68 StartY=12.6253 StartZ=0 EndX=8.28427 EndY=5.22957 EndZ=0
    g14: LineSegment StartX=8.28427 StartY=5.22957 StartZ=0 EndX=8.28427 EndY=-5.22957 EndZ=0
    g15: LineSegment StartX=8.28427 StartY=-5.22957 StartZ=0 EndX=15.68 EndY=-12.6253 EndZ=0
    g16: LineSegment StartX=15.68 StartY=-12.6253 StartZ=0 EndX=15.68 EndY=-4.065 EndZ=0
    g17: LineSegment StartX=15.68 StartY=-4.065 StartZ=0 EndX=20 EndY=-4.065 EndZ=0
    g18: LineSegment StartX=20 StartY=-4.065 StartZ=0 EndX=20 EndY=-20 EndZ=0
    g19: LineSegment StartX=20 StartY=-20 StartZ=0 EndX=4.065 EndY=-20 EndZ=0
    g20: LineSegment StartX=4.065 StartY=-20 StartZ=0 EndX=4.065 EndY=-15.68 EndZ=0
    g21: LineSegment StartX=4.065 StartY=-15.68 StartZ=0 EndX=12.6253 EndY=-15.68 EndZ=0
    g22: LineSegment StartX=12.6253 StartY=-15.68 StartZ=0 EndX=5.22957 EndY=-8.28427 EndZ=0
    g23: LineSegment StartX=5.22957 StartY=-8.28427 StartZ=0 EndX=-5.22957 EndY=-8.28427 EndZ=0
    g24: LineSegment StartX=-5.22957 StartY=-8.28427 StartZ=0 EndX=-12.6253 EndY=-15.68 EndZ=0
    g25: LineSegment StartX=-12.6253 StartY=-15.68 StartZ=0 EndX=-4.065 EndY=-15.68 EndZ=0
    g26: LineSegment StartX=-4.065 StartY=-15.68 StartZ=0 EndX=-4.065 EndY=-20 EndZ=0
    g27: LineSegment StartX=-4.065 StartY=-20 StartZ=0 EndX=-20 EndY=-20 EndZ=0
    g28: LineSegment StartX=-20 StartY=-20 StartZ=0 EndX=-20 EndY=-4.065 EndZ=0
    g29: LineSegment StartX=-20 StartY=-4.065 StartZ=0 EndX=-15.68 EndY=-4.065 EndZ=0
    g30: LineSegment StartX=-15.68 StartY=-4.065 StartZ=0 EndX=-15.68 EndY=-12.6253 EndZ=0
    g31: LineSegment StartX=-15.68 StartY=-12.6253 StartZ=0 EndX=-8.28427 EndY=-5.22957 EndZ=0
    g32: LineSegment StartX=-8.28427 StartY=-5.22957 StartZ=0 EndX=-8.28427 EndY=5.22957 EndZ=0
    g33: LineSegment StartX=-8.28427 StartY=5.22957 StartZ=0 EndX=-15.68 EndY=12.6253 EndZ=0
    g34: LineSegment StartX=-15.68 StartY=12.6253 StartZ=0 EndX=-15.68 EndY=4.065 EndZ=0
    g35: LineSegment StartX=-15.68 StartY=4.065 StartZ=0 EndX=-20 EndY=4.065 EndZ=0
    g36: Circle CenterX=0 CenterY=0 CenterZ=0 NormalX=0 NormalY=0 NormalZ=1 AngleXU=0 Radius=3.405
  constraints (100):
    c: Coincident(g24,g23)
    c: Coincident(g32,g31)
    c: Coincident(g30,g31)
    c: Coincident(g25,g24)
    c: Coincident(g25,g26)
    c: Coincident(g20,g21)
    c: Coincident(g19,g20)
    c: Coincident(g26,g27)
    c: Coincident(g28,g27)
    c: Coincident(g21,g22)
    c: Coincident(g19,g18)
    c: Coincident(g16,g15)
    c: Coincident(g14,g15)
    c: Coincident(g23,g22)
    c: Coincident(g16,g17)
    c: Coincident(g18,g17)
    c: Coincident(g12,g11)
    c: Coincident(g11,g10)
    c: Coincident(g10,g9)
    c: Coincident(g13,g12)
    c: Coincident(g13,g14)
    c: Coincident(g6,g5)
    c: Coincident(g7,g6)
    c: Coincident(g8,g7)
    c: Coincident(g9,g8)
    c: Coincident(g2,g1)
    c: Coincident(g2,g3)
    c: Coincident(g4,g3)
    c: Coincident(g34,g33)
    c: Coincident(g5,g4)
    c: Coincident(g33,g32)
    c: Coincident(g35,g34)
    c: Coincident(g35,g0)
    c: Coincident(g1,g0)
    c: Coincident(g30,g29)
    c: Coincident(g29,g28)
    c: Distance(g10,g0) = 40
    c: Distance(g27,g1) = 40
    c: Tangent(g1,g9)
    c: Tangent(g27,g19)
    c: Tangent(g0,g28)
    c: Tangent(g10,g18)
    c: Horizontal(g1)
    c: Vertical(g0)
    c: Equal(g2,g8)
    c: Equal(g8,g35)
    c: Equal(g35,g29)
    c: Equal(g29,g26)
    c: Equal(g26,g20)
    c: Equal(g20,g17)
    c: Equal(g17,g11)
    c: Vertical(g34)
    c: Vertical(g30)
    c: Vertical(g16)
    c: Vertical(g18)
    c: Vertical(g12)
    c: Vertical(g8)
    c: Vertical(g2)
    c: Vertical(g14)
    c: Vertical(g32)
    c: Horizontal(g35)
    c: Horizontal(g29)
    c: Horizontal(g23)
    c: Horizontal(g19)
    c: Horizontal(g25)
    c: Horizontal(g21)
    c: Horizontal(g7)
    c: Horizontal(g3)
    c: Parallel(g4,g33)
    c: Parallel(g33,g15)
    c: Parallel(g15,g22)
    c: Parallel(g6,g13)
    c: Parallel(g13,g24)
    c: Parallel(g24,g31)
    c: Equal(g23,g24)
    c: Equal(g24,g31)
    c: Equal(g4,g33)
    c: Equal(g6,g13)
    c: Equal(g15,g22)
    c: Angle(g25,g24) = 0.785398
    c: Distance(g8,g2) = 8.13
    c: Distance(g29,g35) = 8.13
    c: Tangent(g35,g11)
    c: Tangent(g17,g29)
    c: Tangent(g2,g26)
    c: Tangent(g8,g20)
    c: Distance(g22,g15) = 4.32
    c: Distance(g13,g6) = 4.32
    c: Distance(g33,g4) = 4.32
    c: Distance(g24,g31) = 4.32
    c: Equal(g32,g14)
    c: Equal(g5,g23)
    c: Equal(g25,g21)
    c: Equal(g34,g30)
    c: Distance(g35,g35) = 4.32
    c: Symmetric(g5,g22,g-1)
    c: Symmetric(g4,g5,g-2)
    c: Equal(g5,g32)
    c: Coincident(g36,g-1)
    c: Diameter(g36) = 6.81
FEATURE [PartDesign::Pad] Pad002
  Direction = (0,0,1)
  Length = 470
  Length2 = 10
  Profile = -> Sketch003
  ReferenceAxis = -> Sketch003 [N_Axis]
  Refine = true
  Suppressed = false
  Type = 0
FEATURE [PartDesign::Body] Body003  label="4040 extrusion @ 470"
  AllowCompound = false
  Group = -> [Sketch003,Pad002]
  Origin = -> Origin005
  Tip = -> Pad002
COMPONENT P10 — recipe-attached ("4040 extrusion @ 616", modeled in this document).
Construction recipe (the document's own serialized feature program — sketch geometry with constraints, then the solid features built on it; lengths are millimeters unless a unit is written):

FEATURE [Sketcher::SketchObject] Sketch002
  ArcFitTolerance = 1e-06
  AttachmentSupport = -> [XY_Plane003]
  FullyConstrained = true
  MakeInternals = false
  MapMode = 5
  sketch-geometry (37):
    g0: LineSegment StartX=-20 StartY=4.065 StartZ=0 EndX=-20 EndY=20 EndZ=0
    g1: LineSegment StartX=-20 StartY=20 StartZ=0 EndX=-4.065 EndY=20 EndZ=0
    g2: LineSegment StartX=-4.065 StartY=20 StartZ=0 EndX=-4.065 EndY=15.68 EndZ=0
    g3: LineSegment StartX=-4.065 StartY=15.68 StartZ=0 EndX=-12.6253 EndY=15.68 EndZ=0
    g4: LineSegment StartX=-12.6253 StartY=15.68 StartZ=0 EndX=-5.22957 EndY=8.28427 EndZ=0
    g5: LineSegment StartX=-5.22957 StartY=8.28427 StartZ=0 EndX=5.22957 EndY=8.28427 EndZ=0
    g6: LineSegment StartX=5.22957 StartY=8.28427 StartZ=0 EndX=12.6253 EndY=15.68 EndZ=0
    g7: LineSegment StartX=12.6253 StartY=15.68 StartZ=0 EndX=4.065 EndY=15.68 EndZ=0
    g8: LineSegment StartX=4.065 StartY=15.68 StartZ=0 EndX=4.065 EndY=20 EndZ=0
    g9: LineSegment StartX=4.065 StartY=20 StartZ=0 EndX=20 EndY=20 EndZ=0
    g10: LineSegment StartX=20 StartY=20 StartZ=0 EndX=20 EndY=4.065 EndZ=0
    g11: LineSegment StartX=20 StartY=4.065 StartZ=0 EndX=15.68 EndY=4.065 EndZ=0
    g12: LineSegment StartX=15.68 StartY=4.065 StartZ=0 EndX=15.68 EndY=12.6253 EndZ=0
    g13: LineSegment StartX=15.68 StartY=12.6253 StartZ=0 EndX=8.28427 EndY=5.22957 EndZ=0
    g14: LineSegment StartX=8.28427 StartY=5.22957 StartZ=0 EndX=8.28427 EndY=-5.22957 EndZ=0
    g15: LineSegment StartX=8.28427 StartY=-5.22957 StartZ=0 EndX=15.68 EndY=-12.6253 EndZ=0
    g16: LineSegment StartX=15.68 StartY=-12.6253 StartZ=0 EndX=15.68 EndY=-4.065 EndZ=0
    g17: LineSegment StartX=15.68 StartY=-4.065 StartZ=0 EndX=20 EndY=-4.065 EndZ=0
    g18: LineSegment StartX=20 StartY=-4.065 StartZ=0 EndX=20 EndY=-20 EndZ=0
    g19: LineSegment StartX=20 StartY=-20 StartZ=0 EndX=4.065 EndY=-20 EndZ=0
    g20: LineSegment StartX=4.065 StartY=-20 StartZ=0 EndX=4.065 EndY=-15.68 EndZ=0
    g21: LineSegment StartX=4.065 StartY=-15.68 StartZ=0 EndX=12.6253 EndY=-15.68 EndZ=0
    g22: LineSegment StartX=12.6253 StartY=-15.68 StartZ=0 EndX=5.22957 EndY=-8.28427 EndZ=0
    g23: LineSegment StartX=5.22957 StartY=-8.28427 StartZ=0 EndX=-5.22957 EndY=-8.28427 EndZ=0
    g24: LineSegment StartX=-5.22957 StartY=-8.28427 StartZ=0 EndX=-12.6253 EndY=-15.68 EndZ=0
    g25: LineSegment StartX=-12.6253 StartY=-15.68 StartZ=0 EndX=-4.065 EndY=-15.68 EndZ=0
    g26: LineSegment StartX=-4.065 StartY=-15.68 StartZ=0 EndX=-4.065 EndY=-20 EndZ=0
    g27: LineSegment StartX=-4.065 StartY=-20 StartZ=0 EndX=-20 EndY=-20 EndZ=0
    g28: LineSegment StartX=-20 StartY=-20 StartZ=0 EndX=-20 EndY=-4.065 EndZ=0
    g29: LineSegment StartX=-20 StartY=-4.065 StartZ=0 EndX=-15.68 EndY=-4.065 EndZ=0
    g30: LineSegment StartX=-15.68 StartY=-4.065 StartZ=0 EndX=-15.68 EndY=-12.6253 EndZ=0
    g31: LineSegment StartX=-15.68 StartY=-12.6253 StartZ=0 EndX=-8.28427 EndY=-5.22957 EndZ=0
    g32: LineSegment StartX=-8.28427 StartY=-5.22957 StartZ=0 EndX=-8.28427 EndY=5.22957 EndZ=0
    g33: LineSegment StartX=-8.28427 StartY=5.22957 StartZ=0 EndX=-15.68 EndY=12.6253 EndZ=0
    g34: LineSegment StartX=-15.68 StartY=12.6253 StartZ=0 EndX=-15.68 EndY=4.065 EndZ=0
    g35: LineSegment StartX=-15.68 StartY=4.065 StartZ=0 EndX=-20 EndY=4.065 EndZ=0
    g36: Circle CenterX=0 CenterY=0 CenterZ=0 NormalX=0 NormalY=0 NormalZ=1 AngleXU=0 Radius=3.405
  constraints (100):
    c: Coincident(g24,g23)
    c: Coincident(g32,g31)
    c: Coincident(g30,g31)
    c: Coincident(g25,g24)
    c: Coincident(g25,g26)
    c: Coincident(g20,g21)
    c: Coincident(g19,g20)
    c: Coincident(g26,g27)
    c: Coincident(g28,g27)
    c: Coincident(g21,g22)
    c: Coincident(g19,g18)
    c: Coincident(g16,g15)
    c: Coincident(g14,g15)
    c: Coincident(g23,g22)
    c: Coincident(g16,g17)
    c: Coincident(g18,g17)
    c: Coincident(g12,g11)
    c: Coincident(g11,g10)
    c: Coincident(g10,g9)
    c: Coincident(g13,g12)
    c: Coincident(g13,g14)
    c: Coincident(g6,g5)
    c: Coincident(g7,g6)
    c: Coincident(g8,g7)
    c: Coincident(g9,g8)
    c: Coincident(g2,g1)
    c: Coincident(g2,g3)
    c: Coincident(g4,g3)
    c: Coincident(g34,g33)
    c: Coincident(g5,g4)
    c: Coincident(g33,g32)
    c: Coincident(g35,g34)
    c: Coincident(g35,g0)
    c: Coincident(g1,g0)
    c: Coincident(g30,g29)
    c: Coincident(g29,g28)
    c: Distance(g10,g0) = 40
    c: Distance(g27,g1) = 40
    c: Tangent(g1,g9)
    c: Tangent(g27,g19)
    c: Tangent(g0,g28)
    c: Tangent(g10,g18)
    c: Horizontal(g1)
    c: Vertical(g0)
    c: Equal(g2,g8)
    c: Equal(g8,g35)
    c: Equal(g35,g29)
    c: Equal(g29,g26)
    c: Equal(g26,g20)
    c: Equal(g20,g17)
    c: Equal(g17,g11)
    c: Vertical(g34)
    c: Vertical(g30)
    c: Vertical(g16)
    c: Vertical(g18)
    c: Vertical(g12)
    c: Vertical(g8)
    c: Vertical(g2)
    c: Vertical(g14)
    c: Vertical(g32)
    c: Horizontal(g35)
    c: Horizontal(g29)
    c: Horizontal(g23)
    c: Horizontal(g19)
    c: Horizontal(g25)
    c: Horizontal(g21)
    c: Horizontal(g7)
    c: Horizontal(g3)
    c: Parallel(g4,g33)
    c: Parallel(g33,g15)
    c: Parallel(g15,g22)
    c: Parallel(g6,g13)
    c: Parallel(g13,g24)
    c: Parallel(g24,g31)
    c: Equal(g23,g24)
    c: Equal(g24,g31)
    c: Equal(g4,g33)
    c: Equal(g6,g13)
    c: Equal(g15,g22)
    c: Angle(g25,g24) = 0.785398
    c: Distance(g8,g2) = 8.13
    c: Distance(g29,g35) = 8.13
    c: Tangent(g35,g11)
    c: Tangent(g17,g29)
    c: Tangent(g2,g26)
    c: Tangent(g8,g20)
    c: Distance(g22,g15) = 4.32
    c: Distance(g13,g6) = 4.32
    c: Distance(g33,g4) = 4.32
    c: Distance(g24,g31) = 4.32
    c: Equal(g32,g14)
    c: Equal(g5,g23)
    c: Equal(g25,g21)
    c: Equal(g34,g30)
    c: Distance(g35,g35) = 4.32
    c: Symmetric(g5,g22,g-1)
    c: Symmetric(g4,g5,g-2)
    c: Equal(g5,g32)
    c: Coincident(g36,g-1)
    c: Diameter(g36) = 6.81
FEATURE [PartDesign::Pad] Pad001
  Direction = (0,0,1)
  Length = 530
  Length2 = 10
  Profile = -> Sketch002
  ReferenceAxis = -> Sketch002 [N_Axis]
  Refine = true
  Suppressed = false
  Type = 0
FEATURE [PartDesign::Body] Body002  label="4040 extrusion @ 530"
  AllowCompound = false
  Group = -> [Sketch002,Pad001]
  Origin = -> Origin003
  Tip = -> Pad001
COMPONENT P11 — recipe-attached ("4040 extrusion @ 615", modeled in this document).
Construction recipe (the document's own serialized feature program — sketch geometry with constraints, then the solid features built on it; lengths are millimeters unless a unit is written):

FEATURE [Sketcher::SketchObject] Sketch001
  ArcFitTolerance = 1e-06
  AttachmentSupport = -> [XY_Plane001]
  FullyConstrained = true
  MakeInternals = false
  MapMode = 5
  sketch-geometry (37):
    g0: LineSegment StartX=-20 StartY=4.065 StartZ=0 EndX=-20 EndY=20 EndZ=0
    g1: LineSegment StartX=-20 StartY=20 StartZ=0 EndX=-4.065 EndY=20 EndZ=0
    g2: LineSegment StartX=-4.065 StartY=20 StartZ=0 EndX=-4.065 EndY=15.68 EndZ=0
    g3: LineSegment StartX=-4.065 StartY=15.68 StartZ=0 EndX=-12.6253 EndY=15.68 EndZ=0
    g4: LineSegment StartX=-12.6253 StartY=15.68 StartZ=0 EndX=-5.22957 EndY=8.28427 EndZ=0
    g5: LineSegment StartX=-5.22957 StartY=8.28427 StartZ=0 EndX=5.22957 EndY=8.28427 EndZ=0
    g6: LineSegment StartX=5.22957 StartY=8.28427 StartZ=0 EndX=12.6253 EndY=15.68 EndZ=0
    g7: LineSegment StartX=12.6253 StartY=15.68 StartZ=0 EndX=4.065 EndY=15.68 EndZ=0
    g8: LineSegment StartX=4.065 StartY=15.68 StartZ=0 EndX=4.065 EndY=20 EndZ=0
    g9: LineSegment StartX=4.065 StartY=20 StartZ=0 EndX=20 EndY=20 EndZ=0
    g10: LineSegment StartX=20 StartY=20 StartZ=0 EndX=20 EndY=4.065 EndZ=0
    g11: LineSegment StartX=20 StartY=4.065 StartZ=0 EndX=15.68 EndY=4.065 EndZ=0
    g12: LineSegment StartX=15.68 StartY=4.065 StartZ=0 EndX=15.68 EndY=12.6253 EndZ=0
    g13: LineSegment StartX=15.68 StartY=12.6253 StartZ=0 EndX=8.28427 EndY=5.22957 EndZ=0
    g14: LineSegment StartX=8.28427 StartY=5.22957 StartZ=0 EndX=8.28427 EndY=-5.22957 EndZ=0
    g15: LineSegment StartX=8.28427 StartY=-5.22957 StartZ=0 EndX=15.68 EndY=-12.6253 EndZ=0
    g16: LineSegment StartX=15.68 StartY=-12.6253 StartZ=0 EndX=15.68 EndY=-4.065 EndZ=0
    g17: LineSegment StartX=15.68 StartY=-4.065 StartZ=0 EndX=20 EndY=-4.065 EndZ=0
    g18: LineSegment StartX=20 StartY=-4.065 StartZ=0 EndX=20 EndY=-20 EndZ=0
    g19: LineSegment StartX=20 StartY=-20 StartZ=0 EndX=4.065 EndY=-20 EndZ=0
    g20: LineSegment StartX=4.065 StartY=-20 StartZ=0 EndX=4.065 EndY=-15.68 EndZ=0
    g21: LineSegment StartX=4.065 StartY=-15.68 StartZ=0 EndX=12.6253 EndY=-15.68 EndZ=0
    g22: LineSegment StartX=12.6253 StartY=-15.68 StartZ=0 EndX=5.22957 EndY=-8.28427 EndZ=0
    g23: LineSegment StartX=5.22957 StartY=-8.28427 StartZ=0 EndX=-5.22957 EndY=-8.28427 EndZ=0
    g24: LineSegment StartX=-5.22957 StartY=-8.28427 StartZ=0 EndX=-12.6253 EndY=-15.68 EndZ=0
    g25: LineSegment StartX=-12.6253 StartY=-15.68 StartZ=0 EndX=-4.065 EndY=-15.68 EndZ=0
    g26: LineSegment StartX=-4.065 StartY=-15.68 StartZ=0 EndX=-4.065 EndY=-20 EndZ=0
    g27: LineSegment StartX=-4.065 StartY=-20 StartZ=0 EndX=-20 EndY=-20 EndZ=0
    g28: LineSegment StartX=-20 StartY=-20 StartZ=0 EndX=-20 EndY=-4.065 EndZ=0
    g29: LineSegment StartX=-20 StartY=-4.065 StartZ=0 EndX=-15.68 EndY=-4.065 EndZ=0
    g30: LineSegment StartX=-15.68 StartY=-4.065 StartZ=0 EndX=-15.68 EndY=-12.6253 EndZ=0
    g31: LineSegment StartX=-15.68 StartY=-12.6253 StartZ=0 EndX=-8.28427 EndY=-5.22957 EndZ=0
    g32: LineSegment StartX=-8.28427 StartY=-5.22957 StartZ=0 EndX=-8.28427 EndY=5.22957 EndZ=0
    g33: LineSegment StartX=-8.28427 StartY=5.22957 StartZ=0 EndX=-15.68 EndY=12.6253 EndZ=0
    g34: LineSegment StartX=-15.68 StartY=12.6253 StartZ=0 EndX=-15.68 EndY=4.065 EndZ=0
    g35: LineSegment StartX=-15.68 StartY=4.065 StartZ=0 EndX=-20 EndY=4.065 EndZ=0
    g36: Circle CenterX=0 CenterY=0 CenterZ=0 NormalX=0 NormalY=0 NormalZ=1 AngleXU=0 Radius=3.405
  constraints (100):
    c: Coincident(g24,g23)
    c: Coincident(g32,g31)
    c: Coincident(g30,g31)
    c: Coincident(g25,g24)
    c: Coincident(g25,g26)
    c: Coincident(g20,g21)
    c: Coincident(g19,g20)
    c: Coincident(g26,g27)
    c: Coincident(g28,g27)
    c: Coincident(g21,g22)
    c: Coincident(g19,g18)
    c: Coincident(g16,g15)
    c: Coincident(g14,g15)
    c: Coincident(g23,g22)
    c: Coincident(g16,g17)
    c: Coincident(g18,g17)
    c: Coincident(g12,g11)
    c: Coincident(g11,g10)
    c: Coincident(g10,g9)
    c: Coincident(g13,g12)
    c: Coincident(g13,g14)
    c: Coincident(g6,g5)
    c: Coincident(g7,g6)
    c: Coincident(g8,g7)
    c: Coincident(g9,g8)
    c: Coincident(g2,g1)
    c: Coincident(g2,g3)
    c: Coincident(g4,g3)
    c: Coincident(g34,g33)
    c: Coincident(g5,g4)
    c: Coincident(g33,g32)
    c: Coincident(g35,g34)
    c: Coincident(g35,g0)
    c: Coincident(g1,g0)
    c: Coincident(g30,g29)
    c: Coincident(g29,g28)
    c: Distance(g10,g0) = 40
    c: Distance(g27,g1) = 40
    c: Tangent(g1,g9)
    c: Tangent(g27,g19)
    c: Tangent(g0,g28)
    c: Tangent(g10,g18)
    c: Horizontal(g1)
    c: Vertical(g0)
    c: Equal(g2,g8)
    c: Equal(g8,g35)
    c: Equal(g35,g29)
    c: Equal(g29,g26)
    c: Equal(g26,g20)
    c: Equal(g20,g17)
    c: Equal(g17,g11)
    c: Vertical(g34)
    c: Vertical(g30)
    c: Vertical(g16)
    c: Vertical(g18)
    c: Vertical(g12)
    c: Vertical(g8)
    c: Vertical(g2)
    c: Vertical(g14)
    c: Vertical(g32)
    c: Horizontal(g35)
    c: Horizontal(g29)
    c: Horizontal(g23)
    c: Horizontal(g19)
    c: Horizontal(g25)
    c: Horizontal(g21)
    c: Horizontal(g7)
    c: Horizontal(g3)
    c: Parallel(g4,g33)
    c: Parallel(g33,g15)
    c: Parallel(g15,g22)
    c: Parallel(g6,g13)
    c: Parallel(g13,g24)
    c: Parallel(g24,g31)
    c: Equal(g23,g24)
    c: Equal(g24,g31)
    c: Equal(g4,g33)
    c: Equal(g6,g13)
    c: Equal(g15,g22)
    c: Angle(g25,g24) = 0.785398
    c: Distance(g8,g2) = 8.13
    c: Distance(g29,g35) = 8.13
    c: Tangent(g35,g11)
    c: Tangent(g17,g29)
    c: Tangent(g2,g26)
    c: Tangent(g8,g20)
    c: Distance(g22,g15) = 4.32
    c: Distance(g13,g6) = 4.32
    c: Distance(g33,g4) = 4.32
    c: Distance(g24,g31) = 4.32
    c: Equal(g32,g14)
    c: Equal(g5,g23)
    c: Equal(g25,g21)
    c: Equal(g34,g30)
    c: Distance(g35,g35) = 4.32
    c: Symmetric(g5,g22,g-1)
    c: Symmetric(g4,g5,g-2)
    c: Equal(g5,g32)
    c: Coincident(g36,g-1)
    c: Diameter(g36) = 6.81
FEATURE [PartDesign::Pad] Pad
  Direction = (0,0,1)
  Length = 610
  Length2 = 10
  Profile = -> Sketch001
  ReferenceAxis = -> Sketch001 [N_Axis]
  Refine = true
  Suppressed = false
  Type = 0
FEATURE [PartDesign::Body] Body001  label="4040 extrusion @ 610"
  AllowCompound = false
  Group = -> [Sketch001,Pad]
  Origin = -> Origin001
  Tip = -> Pad
COMPONENT P12 — same part as P10; its construction recipe is shown at P10.
COMPONENT P13 — same part as P11; its construction recipe is shown at P11.
COMPONENT P14 — same part as P9; its construction recipe is shown at P9.
COMPONENT P15 — same part as P9; its construction recipe is shown at P9.
COMPONENT P16 — same part as P9; its construction recipe is shown at P9.
COMPONENT P17 — same part as P11; its construction recipe is shown at P11.
COMPONENT P18 — same part as P11; its construction recipe is shown at P11.
COMPONENT P19 — same part as P10; its construction recipe is shown at P10.
COMPONENT P20 — same part as P10; its construction recipe is shown at P10.
COMPONENT P21 — recipe-attached ("8040 extrusion @ 533", modeled in this document).
Construction recipe (the document's own serialized feature program — sketch geometry with constraints, then the solid features built on it; lengths are millimeters unless a unit is written):

FEATURE [Sketcher::SketchObject] Sketch004
  ArcFitTolerance = 1e-06
  AttachmentSupport = -> [XY_Plane006]
  FullyConstrained = true
  MakeInternals = false
  MapMode = 5
  sketch-geometry (70):
    g0: LineSegment StartX=-20 StartY=4.065 StartZ=0 EndX=-20 EndY=20 EndZ=0
    g1: LineSegment StartX=-20 StartY=20 StartZ=0 EndX=-4.065 EndY=20 EndZ=0
    g2: LineSegment StartX=-4.065 StartY=20 StartZ=0 EndX=-4.065 EndY=15.68 EndZ=0
    g3: LineSegment StartX=-4.065 StartY=15.68 StartZ=0 EndX=-12.6253 EndY=15.68 EndZ=0
    g4: LineSegment StartX=-12.6253 StartY=15.68 StartZ=0 EndX=-5.22957 EndY=8.28427 EndZ=0
    g5: LineSegment StartX=-5.22957 StartY=8.28427 StartZ=0 EndX=5.22957 EndY=8.28427 EndZ=0
    g6: LineSegment StartX=5.22957 StartY=8.28427 StartZ=0 EndX=12.6253 EndY=15.68 EndZ=0
    g7: LineSegment StartX=12.6253 StartY=15.68 StartZ=0 EndX=4.065 EndY=15.68 EndZ=0
    g8: LineSegment StartX=4.065 StartY=15.68 StartZ=0 EndX=4.065 EndY=20 EndZ=0
    g9: LineSegment StartX=4.065 StartY=20 StartZ=0 EndX=20 EndY=20 EndZ=0
    g10: LineSegment StartX=20 StartY=4.065 StartZ=0 EndX=15.68 EndY=4.065 EndZ=0
    g11: LineSegment StartX=15.68 StartY=4.065 StartZ=0 EndX=15.68 EndY=12.6253 EndZ=0
    g12: LineSegment StartX=15.68 StartY=12.6253 StartZ=0 EndX=8.28427 EndY=5.22957 EndZ=0
    g13: LineSegment StartX=8.28427 StartY=5.22957 StartZ=0 EndX=8.28427 EndY=-5.22957 EndZ=0
    g14: LineSegment StartX=8.28427 StartY=-5.22957 StartZ=0 EndX=15.68 EndY=-12.6253 EndZ=0
    g15: LineSegment StartX=15.68 StartY=-12.6253 StartZ=0 EndX=15.68 EndY=-4.065 EndZ=0
    g16: LineSegment StartX=15.68 StartY=-4.065 StartZ=0 EndX=20 EndY=-4.065 EndZ=0
    g17: LineSegment StartX=20 StartY=-20 StartZ=0 EndX=4.065 EndY=-20 EndZ=0
    g18: LineSegment StartX=4.065 StartY=-20 StartZ=0 EndX=4.065 EndY=-15.68 EndZ=0
    g19: LineSegment StartX=4.065 StartY=-15.68 StartZ=0 EndX=12.6253 EndY=-15.68 EndZ=0
    g20: LineSegment StartX=12.6253 StartY=-15.68 StartZ=0 EndX=5.22957 EndY=-8.28427 EndZ=0
    g21: LineSegment StartX=5.22957 StartY=-8.28427 StartZ=0 EndX=-5.22957 EndY=-8.28427 EndZ=0
    g22: LineSegment StartX=-5.22957 StartY=-8.28427 StartZ=0 EndX=-12.6253 EndY=-15.68 EndZ=0
    g23: LineSegment StartX=-12.6253 StartY=-15.68 StartZ=0 EndX=-4.065 EndY=-15.68 EndZ=0
    g24: LineSegment StartX=-4.065 StartY=-15.68 StartZ=0 EndX=-4.065 EndY=-20 EndZ=0
    g25: LineSegment StartX=-4.065 StartY=-20 StartZ=0 EndX=-20 EndY=-20 EndZ=0
    g26: LineSegment StartX=-20 StartY=-20 StartZ=0 EndX=-20 EndY=-4.065 EndZ=0
    g27: LineSegment StartX=-20 StartY=-4.065 StartZ=0 EndX=-15.68 EndY=-4.065 EndZ=0
    g28: LineSegment StartX=-15.68 StartY=-4.065 StartZ=0 EndX=-15.68 EndY=-12.6253 EndZ=0
    g29: LineSegment StartX=-15.68 StartY=-12.6253 StartZ=0 EndX=-8.28427 EndY=-5.22957 EndZ=0
    g30: LineSegment StartX=-8.28427 StartY=-5.22957 StartZ=0 EndX=-8.28427 EndY=5.22957 EndZ=0
    g31: LineSegment StartX=-8.28427 StartY=5.22957 StartZ=0 EndX=-15.68 EndY=12.6253 EndZ=0
    g32: LineSegment StartX=-15.68 StartY=12.6253 StartZ=0 EndX=-15.68 EndY=4.065 EndZ=0
    g33: LineSegment StartX=-15.68 StartY=4.065 StartZ=0 EndX=-20 EndY=4.065 EndZ=0
    g34: Circle CenterX=0 CenterY=0 CenterZ=0 NormalX=0 NormalY=0 NormalZ=1 AngleXU=0 Radius=3.405
    g35: LineSegment StartX=20 StartY=20 StartZ=0 EndX=35.935 EndY=20 EndZ=0
    g36: LineSegment StartX=35.935 StartY=20 StartZ=0 EndX=35.935 EndY=15.68 EndZ=0
    g37: LineSegment StartX=35.935 StartY=15.68 StartZ=0 EndX=27.3747 EndY=15.68 EndZ=0
    g38: LineSegment StartX=27.3747 StartY=15.68 StartZ=0 EndX=34.7704 EndY=8.28427 EndZ=0
    g39: LineSegment StartX=34.7704 StartY=8.28427 StartZ=0 EndX=45.2296 EndY=8.28427 EndZ=0
    g40: LineSegment StartX=45.2296 StartY=8.28427 StartZ=0 EndX=52.6253 EndY=15.68 EndZ=0
    g41: LineSegment StartX=52.6253 StartY=15.68 StartZ=0 EndX=44.065 EndY=15.68 EndZ=0
    g42: LineSegment StartX=44.065 StartY=15.68 StartZ=0 EndX=44.065 EndY=20 EndZ=0
    g43: LineSegment StartX=44.065 StartY=20 StartZ=0 EndX=60 EndY=20 EndZ=0
    g44: LineSegment StartX=60 StartY=20 StartZ=0 EndX=60 EndY=4.065 EndZ=0
    g45: LineSegment StartX=60 StartY=4.065 StartZ=0 EndX=55.68 EndY=4.065 EndZ=0
    g46: LineSegment StartX=55.68 StartY=4.065 StartZ=0 EndX=55.68 EndY=12.6253 EndZ=0
    g47: LineSegment StartX=55.68 StartY=12.6253 StartZ=0 EndX=48.2843 EndY=5.22957 EndZ=0
    g48: LineSegment StartX=48.2843 StartY=5.22957 StartZ=0 EndX=48.2843 EndY=-5.22957 EndZ=0
    g49: LineSegment StartX=48.2843 StartY=-5.22957 StartZ=0 EndX=55.68 EndY=-12.6253 EndZ=0
    g50: LineSegment StartX=55.68 StartY=-12.6253 StartZ=0 EndX=55.68 EndY=-4.065 EndZ=0
    g51: LineSegment StartX=55.68 StartY=-4.065 StartZ=0 EndX=60 EndY=-4.065 EndZ=0
    g52: LineSegment StartX=60 StartY=-4.065 StartZ=0 EndX=60 EndY=-20 EndZ=0
    g53: LineSegment StartX=60 StartY=-20 StartZ=0 EndX=44.065 EndY=-20 EndZ=0
    g54: LineSegment StartX=44.065 StartY=-20 StartZ=0 EndX=44.065 EndY=-15.68 EndZ=0
    g55: LineSegment StartX=44.065 StartY=-15.68 StartZ=0 EndX=52.6253 EndY=-15.68 EndZ=0
    g56: LineSegment StartX=52.6253 StartY=-15.68 StartZ=0 EndX=45.2296 EndY=-8.28427 EndZ=0
    g57: LineSegment StartX=45.2296 StartY=-8.28427 StartZ=0 EndX=34.7704 EndY=-8.28427 EndZ=0
    g58: LineSegment StartX=34.7704 StartY=-8.28427 StartZ=0 EndX=27.3747 EndY=-15.68 EndZ=0
    g59: LineSegment StartX=27.3747 StartY=-15.68 StartZ=0 EndX=35.935 EndY=-15.68 EndZ=0
    g60: LineSegment StartX=35.935 StartY=-15.68 StartZ=0 EndX=35.935 EndY=-20 EndZ=0
    g61: LineSegment StartX=35.935 StartY=-20 StartZ=0 EndX=20 EndY=-20 EndZ=0
    g62: LineSegment StartX=24.32 StartY=12.6253 StartZ=0 EndX=24.32 EndY=4.065 EndZ=0
    g63: LineSegment StartX=24.32 StartY=4.065 StartZ=0 EndX=20 EndY=4.065 EndZ=0
    g64: LineSegment StartX=20 StartY=-4.065 StartZ=0 EndX=24.32 EndY=-4.065 EndZ=0
    g65: LineSegment StartX=24.32 StartY=-4.065 StartZ=0 EndX=24.32 EndY=-12.6253 EndZ=0
    g66: LineSegment StartX=24.32 StartY=-12.6253 StartZ=0 EndX=31.7157 EndY=-5.22957 EndZ=0
    g67: LineSegment StartX=31.7157 StartY=-5.22957 StartZ=0 EndX=31.7157 EndY=5.22957 EndZ=0
    g68: LineSegment StartX=31.7157 StartY=5.22957 StartZ=0 EndX=24.32 EndY=12.6253 EndZ=0
    g69: Circle CenterX=40 CenterY=0 CenterZ=0 NormalX=0 NormalY=0 NormalZ=1 AngleXU=0 Radius=3.405
  constraints (200):
    c: Coincident(g22,g21)
    c: Coincident(g30,g29)
    c: Coincident(g28,g29)
    c: Coincident(g23,g22)
    c: Coincident(g23,g24)
    c: Coincident(g18,g19)
    c: Coincident(g17,g18)
    c: Coincident(g24,g25)
    c: Coincident(g26,g25)
    c: Coincident(g19,g20)
    c: Coincident(g15,g14)
    c: Coincident(g13,g14)
    c: Coincident(g21,g20)
    c: Coincident(g15,g16)
    c: Coincident(g11,g10)
    c: Coincident(g12,g11)
    c: Coincident(g12,g13)
    c: Coincident(g6,g5)
    c: Coincident(g7,g6)
    c: Coincident(g8,g7)
    c: Coincident(g9,g8)
    c: Coincident(g2,g1)
    c: Coincident(g2,g3)
    c: Coincident(g4,g3)
    c: Coincident(g32,g31)
    c: Coincident(g5,g4)
    c: Coincident(g31,g30)
    c: Coincident(g33,g32)
    c: Coincident(g33,g0)
    c: Coincident(g1,g0)
    c: Coincident(g28,g27)
    c: Coincident(g27,g26)
    c: Distance(g9,g0) = 40
    c: Distance(g25,g1) = 40
    c: Tangent(g1,g9)
    c: Tangent(g25,g17)
    c: Tangent(g0,g26)
    c: Horizontal(g1)
    c: Vertical(g0)
    c: Equal(g2,g8)
    c: Equal(g8,g33)
    c: Equal(g33,g27)
    c: Equal(g27,g24)
    c: Equal(g24,g18)
    c: Equal(g18,g16)
    c: Equal(g16,g10)
    c: Vertical(g32)
    c: Vertical(g28)
    c: Vertical(g15)
    c: Vertical(g11)
    c: Vertical(g8)
    c: Vertical(g2)
    c: Vertical(g13)
    c: Vertical(g30)
    c: Horizontal(g33)
    c: Horizontal(g27)
    c: Horizontal(g21)
    c: Horizontal(g17)
    c: Horizontal(g23)
    c: Horizontal(g19)
    c: Horizontal(g7)
    c: Horizontal(g3)
    c: Parallel(g4,g31)
    c: Parallel(g31,g14)
    c: Parallel(g14,g20)
    c: Parallel(g6,g12)
    c: Parallel(g12,g22)
    c: Parallel(g22,g29)
    c: Equal(g21,g22)
    c: Equal(g22,g29)
    c: Equal(g4,g31)
    c: Equal(g6,g12)
    c: Equal(g14,g20)
    c: Angle(g23,g22) = 0.785398
    c: Distance(g8,g2) = 8.13
    c: Distance(g27,g33) = 8.13
    c: Tangent(g33,g10)
    c: Tangent(g16,g27)
    c: Tangent(g2,g24)
    c: Tangent(g8,g18)
    c: Distance(g20,g14) = 4.32
    c: Distance(g12,g6) = 4.32
    c: Distance(g31,g4) = 4.32
    c: Distance(g22,g29) = 4.32
    c: Equal(g30,g13)
    c: Equal(g5,g21)
    c: Equal(g23,g19)
    c: Equal(g32,g28)
    c: Distance(g33,g33) = 4.32
    c: Symmetric(g5,g20,g-1)
    c: Symmetric(g4,g5,g-2)
    c: Equal(g5,g30)
    c: Coincident(g34,g-1)
    c: Diameter(g34) = 6.81
    c: Coincident(g35,g9)
    c: Coincident(g36,g35)
    c: Coincident(g37,g36)
    c: Horizontal(g37)
    c: Coincident(g38,g37)
    c: Coincident(g39,g38)
    c: Horizontal(g39)
    c: Coincident(g41,g40)
    c: Vertical(g44)
    c: Coincident(g45,g44)
    c: Coincident(g48,g47)
    c: Vertical(g48)
    c: Coincident(g49,g48)
    c: Vertical(g50)
    c: Horizontal(g51)
    c: Coincident(g52,g51)
    c: Vertical(g52)
    c: Coincident(g53,g52)
    c: Coincident(g55,g54)
    c: Coincident(g57,g56)
    c: Horizontal(g57)
    c: Coincident(g58,g57)
    c: Coincident(g59,g58)
    c: Horizontal(g59)
    c: Coincident(g61,g60)
    c: Coincident(g61,g17)
    c: Coincident(g63,g10)
    c: Coincident(g64,g16)
    c: Coincident(g65,g64)
    c: Coincident(g66,g65)
    c: Coincident(g67,g66)
    c: Coincident(g68,g67)
    c: Coincident(g68,g62)
    c: PointOnObject(g69,g-1)
    c: Coincident(g43,g42)
    c: Coincident(g43,g44)
    c: Coincident(g41,g42)
    c: Coincident(g39,g40)
    c: Coincident(g46,g47)
    c: Coincident(g46,g45)
    c: Coincident(g50,g51)
    c: Coincident(g49,g50)
    c: Coincident(g54,g53)
    c: Coincident(g56,g55)
    c: Coincident(g59,g60)
    c: Coincident(g62,g63)
    c: Equal(g34,g69)
    c: Equal(g39,g67)
    c: Equal(g67,g57)
    c: Equal(g57,g48)
    c: Equal(g48,g13)
    c: Equal(g38,g68)
    c: Equal(g68,g66)
    c: Equal(g66,g58)
    c: Equal(g58,g56)
    c: Equal(g56,g49)
    c: Equal(g49,g47)
    c: Equal(g47,g40)
    c: Equal(g40,g12)
    c: Equal(g10,g63)
    c: Equal(g16,g64)
    c: Equal(g64,g45)
    c: Equal(g45,g51)
    c: Equal(g51,g42)
    c: Equal(g42,g36)
    c: Equal(g36,g60)
    c: Equal(g60,g54)
    c: Parallel(g47,g40)
    c: Parallel(g38,g68)
    c: Parallel(g66,g58)
    c: Parallel(g49,g56)
    c: Parallel(g56,g68)
    c: Parallel(g40,g66)
    c: Horizontal(g35)
    c: Horizontal(g43)
    c: Horizontal(g45)
    c: Horizontal(g53)
    c: Horizontal(g61)
    c: Horizontal(g64)
    c: Horizontal(g63)
    c: Horizontal(g41)
    c: Vertical(g42)
    c: Vertical(g36)
    c: Vertical(g62)
    c: Vertical(g65)
    c: Vertical(g60)
    c: Vertical(g54)
    c: Vertical(g46)
    c: Horizontal(g55)
    c: Vertical(g67)
    c: Equal(g7,g37)
    c: Equal(g37,g41)
    c: Equal(g41,g46)
    c: Equal(g46,g55)
    c: Equal(g55,g59)
    c: Equal(g59,g65)
    c: Equal(g65,g62)
    c: Equal(g55,g50)
    c: Parallel(g40,g6)
    c: Distance(g9,g44) = 40
    c: DistanceX(g34,g69) = 40
    c: Equal(g35,g43)
    c: Equal(g43,g9)
    c: Equal(g44,g52)
    c: Equal(g53,g61)
    c: Equal(g61,g17)
FEATURE [PartDesign::Pad] Pad003
  Direction = (0,0,1)
  Length = 530
  Length2 = 10
  Profile = -> Sketch004
  ReferenceAxis = -> Sketch004 [N_Axis]
  Refine = true
  Suppressed = false
  Type = 0
FEATURE [PartDesign::Body] Body004  label="8040 extrusion @ 530"
  AllowCompound = false
  Group = -> [Sketch004,Pad003]
  Origin = -> Origin006
  Tip = -> Pad003
COMPONENT P22 — same part as P21; its construction recipe is shown at P21.
COMPONENT P23 — same part as P8; its construction recipe is shown at P8.
COMPONENT P24 — recipe-attached ("8040 extrusion @ 535", modeled in this document).
Construction recipe (the document's own serialized feature program — sketch geometry with constraints, then the solid features built on it; lengths are millimeters unless a unit is written):

FEATURE [Sketcher::SketchObject] Sketch005
  ArcFitTolerance = 1e-06
  AttachmentSupport = -> [XY_Plane007]
  FullyConstrained = true
  MakeInternals = false
  MapMode = 5
  sketch-geometry (70):
    g0: LineSegment StartX=-20 StartY=4.065 StartZ=0 EndX=-20 EndY=20 EndZ=0
    g1: LineSegment StartX=-20 StartY=20 StartZ=0 EndX=-4.065 EndY=20 EndZ=0
    g2: LineSegment StartX=-4.065 StartY=20 StartZ=0 EndX=-4.065 EndY=15.68 EndZ=0
    g3: LineSegment StartX=-4.065 StartY=15.68 StartZ=0 EndX=-12.6253 EndY=15.68 EndZ=0
    g4: LineSegment StartX=-12.6253 StartY=15.68 StartZ=0 EndX=-5.22957 EndY=8.28427 EndZ=0
    g5: LineSegment StartX=-5.22957 StartY=8.28427 StartZ=0 EndX=5.22957 EndY=8.28427 EndZ=0
    g6: LineSegment StartX=5.22957 StartY=8.28427 StartZ=0 EndX=12.6253 EndY=15.68 EndZ=0
    g7: LineSegment StartX=12.6253 StartY=15.68 StartZ=0 EndX=4.065 EndY=15.68 EndZ=0
    g8: LineSegment StartX=4.065 StartY=15.68 StartZ=0 EndX=4.065 EndY=20 EndZ=0
    g9: LineSegment StartX=4.065 StartY=20 StartZ=0 EndX=20 EndY=20 EndZ=0
    g10: LineSegment StartX=20 StartY=4.065 StartZ=0 EndX=15.68 EndY=4.065 EndZ=0
    g11: LineSegment StartX=15.68 StartY=4.065 StartZ=0 EndX=15.68 EndY=12.6253 EndZ=0
    g12: LineSegment StartX=15.68 StartY=12.6253 StartZ=0 EndX=8.28427 EndY=5.22957 EndZ=0
    g13: LineSegment StartX=8.28427 StartY=5.22957 StartZ=0 EndX=8.28427 EndY=-5.22957 EndZ=0
    g14: LineSegment StartX=8.28427 StartY=-5.22957 StartZ=0 EndX=15.68 EndY=-12.6253 EndZ=0
    g15: LineSegment StartX=15.68 StartY=-12.6253 StartZ=0 EndX=15.68 EndY=-4.065 EndZ=0
    g16: LineSegment StartX=15.68 StartY=-4.065 StartZ=0 EndX=20 EndY=-4.065 EndZ=0
    g17: LineSegment StartX=20 StartY=-20 StartZ=0 EndX=4.065 EndY=-20 EndZ=0
    g18: LineSegment StartX=4.065 StartY=-20 StartZ=0 EndX=4.065 EndY=-15.68 EndZ=0
    g19: LineSegment StartX=4.065 StartY=-15.68 StartZ=0 EndX=12.6253 EndY=-15.68 EndZ=0
    g20: LineSegment StartX=12.6253 StartY=-15.68 StartZ=0 EndX=5.22957 EndY=-8.28427 EndZ=0
    g21: LineSegment StartX=5.22957 StartY=-8.28427 StartZ=0 EndX=-5.22957 EndY=-8.28427 EndZ=0
    g22: LineSegment StartX=-5.22957 StartY=-8.28427 StartZ=0 EndX=-12.6253 EndY=-15.68 EndZ=0
    g23: LineSegment StartX=-12.6253 StartY=-15.68 StartZ=0 EndX=-4.065 EndY=-15.68 EndZ=0
    g24: LineSegment StartX=-4.065 StartY=-15.68 StartZ=0 EndX=-4.065 EndY=-20 EndZ=0
    g25: LineSegment StartX=-4.065 StartY=-20 StartZ=0 EndX=-20 EndY=-20 EndZ=0
    g26: LineSegment StartX=-20 StartY=-20 StartZ=0 EndX=-20 EndY=-4.065 EndZ=0
    g27: LineSegment StartX=-20 StartY=-4.065 StartZ=0 EndX=-15.68 EndY=-4.065 EndZ=0
    g28: LineSegment StartX=-15.68 StartY=-4.065 StartZ=0 EndX=-15.68 EndY=-12.6253 EndZ=0
    g29: LineSegment StartX=-15.68 StartY=-12.6253 StartZ=0 EndX=-8.28427 EndY=-5.22957 EndZ=0
    g30: LineSegment StartX=-8.28427 StartY=-5.22957 StartZ=0 EndX=-8.28427 EndY=5.22957 EndZ=0
    g31: LineSegment StartX=-8.28427 StartY=5.22957 StartZ=0 EndX=-15.68 EndY=12.6253 EndZ=0
    g32: LineSegment StartX=-15.68 StartY=12.6253 StartZ=0 EndX=-15.68 EndY=4.065 EndZ=0
    g33: LineSegment StartX=-15.68 StartY=4.065 StartZ=0 EndX=-20 EndY=4.065 EndZ=0
    g34: Circle CenterX=0 CenterY=0 CenterZ=0 NormalX=0 NormalY=0 NormalZ=1 AngleXU=0 Radius=3.405
    g35: LineSegment StartX=20 StartY=20 StartZ=0 EndX=35.935 EndY=20 EndZ=0
    g36: LineSegment StartX=35.935 StartY=20 StartZ=0 EndX=35.935 EndY=15.68 EndZ=0
    g37: LineSegment StartX=35.935 StartY=15.68 StartZ=0 EndX=27.3747 EndY=15.68 EndZ=0
    g38: LineSegment StartX=27.3747 StartY=15.68 StartZ=0 EndX=34.7704 EndY=8.28427 EndZ=0
    g39: LineSegment StartX=34.7704 StartY=8.28427 StartZ=0 EndX=45.2296 EndY=8.28427 EndZ=0
    g40: LineSegment StartX=45.2296 StartY=8.28427 StartZ=0 EndX=52.6253 EndY=15.68 EndZ=0
    g41: LineSegment StartX=52.6253 StartY=15.68 StartZ=0 EndX=44.065 EndY=15.68 EndZ=0
    g42: LineSegment StartX=44.065 StartY=15.68 StartZ=0 EndX=44.065 EndY=20 EndZ=0
    g43: LineSegment StartX=44.065 StartY=20 StartZ=0 EndX=60 EndY=20 EndZ=0
    g44: LineSegment StartX=60 StartY=20 StartZ=0 EndX=60 EndY=4.065 EndZ=0
    g45: LineSegment StartX=60 StartY=4.065 StartZ=0 EndX=55.68 EndY=4.065 EndZ=0
    g46: LineSegment StartX=55.68 StartY=4.065 StartZ=0 EndX=55.68 EndY=12.6253 EndZ=0
    g47: LineSegment StartX=55.68 StartY=12.6253 StartZ=0 EndX=48.2843 EndY=5.22957 EndZ=0
    g48: LineSegment StartX=48.2843 StartY=5.22957 StartZ=0 EndX=48.2843 EndY=-5.22957 EndZ=0
    g49: LineSegment StartX=48.2843 StartY=-5.22957 StartZ=0 EndX=55.68 EndY=-12.6253 EndZ=0
    g50: LineSegment StartX=55.68 StartY=-12.6253 StartZ=0 EndX=55.68 EndY=-4.065 EndZ=0
    g51: LineSegment StartX=55.68 StartY=-4.065 StartZ=0 EndX=60 EndY=-4.065 EndZ=0
    g52: LineSegment StartX=60 StartY=-4.065 StartZ=0 EndX=60 EndY=-20 EndZ=0
    g53: LineSegment StartX=60 StartY=-20 StartZ=0 EndX=44.065 EndY=-20 EndZ=0
    g54: LineSegment StartX=44.065 StartY=-20 StartZ=0 EndX=44.065 EndY=-15.68 EndZ=0
    g55: LineSegment StartX=44.065 StartY=-15.68 StartZ=0 EndX=52.6253 EndY=-15.68 EndZ=0
    g56: LineSegment StartX=52.6253 StartY=-15.68 StartZ=0 EndX=45.2296 EndY=-8.28427 EndZ=0
    g57: LineSegment StartX=45.2296 StartY=-8.28427 StartZ=0 EndX=34.7704 EndY=-8.28427 EndZ=0
    g58: LineSegment StartX=34.7704 StartY=-8.28427 StartZ=0 EndX=27.3747 EndY=-15.68 EndZ=0
    g59: LineSegment StartX=27.3747 StartY=-15.68 StartZ=0 EndX=35.935 EndY=-15.68 EndZ=0
    g60: LineSegment StartX=35.935 StartY=-15.68 StartZ=0 EndX=35.935 EndY=-20 EndZ=0
    g61: LineSegment StartX=35.935 StartY=-20 StartZ=0 EndX=20 EndY=-20 EndZ=0
    g62: LineSegment StartX=24.32 StartY=12.6253 StartZ=0 EndX=24.32 EndY=4.065 EndZ=0
    g63: LineSegment StartX=24.32 StartY=4.065 StartZ=0 EndX=20 EndY=4.065 EndZ=0
    g64: LineSegment StartX=20 StartY=-4.065 StartZ=0 EndX=24.32 EndY=-4.065 EndZ=0
    g65: LineSegment StartX=24.32 StartY=-4.065 StartZ=0 EndX=24.32 EndY=-12.6253 EndZ=0
    g66: LineSegment StartX=24.32 StartY=-12.6253 StartZ=0 EndX=31.7157 EndY=-5.22957 EndZ=0
    g67: LineSegment StartX=31.7157 StartY=-5.22957 StartZ=0 EndX=31.7157 EndY=5.22957 EndZ=0
    g68: LineSegment StartX=31.7157 StartY=5.22957 StartZ=0 EndX=24.32 EndY=12.6253 EndZ=0
    g69: Circle CenterX=40 CenterY=0 CenterZ=0 NormalX=0 NormalY=0 NormalZ=1 AngleXU=0 Radius=3.405
  constraints (200):
    c: Coincident(g22,g21)
    c: Coincident(g30,g29)
    c: Coincident(g28,g29)
    c: Coincident(g23,g22)
    c: Coincident(g23,g24)
    c: Coincident(g18,g19)
    c: Coincident(g17,g18)
    c: Coincident(g24,g25)
    c: Coincident(g26,g25)
    c: Coincident(g19,g20)
    c: Coincident(g15,g14)
    c: Coincident(g13,g14)
    c: Coincident(g21,g20)
    c: Coincident(g15,g16)
    c: Coincident(g11,g10)
    c: Coincident(g12,g11)
    c: Coincident(g12,g13)
    c: Coincident(g6,g5)
    c: Coincident(g7,g6)
    c: Coincident(g8,g7)
    c: Coincident(g9,g8)
    c: Coincident(g2,g1)
    c: Coincident(g2,g3)
    c: Coincident(g4,g3)
    c: Coincident(g32,g31)
    c: Coincident(g5,g4)
    c: Coincident(g31,g30)
    c: Coincident(g33,g32)
    c: Coincident(g33,g0)
    c: Coincident(g1,g0)
    c: Coincident(g28,g27)
    c: Coincident(g27,g26)
    c: Distance(g9,g0) = 40
    c: Distance(g25,g1) = 40
    c: Tangent(g1,g9)
    c: Tangent(g25,g17)
    c: Tangent(g0,g26)
    c: Horizontal(g1)
    c: Vertical(g0)
    c: Equal(g2,g8)
    c: Equal(g8,g33)
    c: Equal(g33,g27)
    c: Equal(g27,g24)
    c: Equal(g24,g18)
    c: Equal(g18,g16)
    c: Equal(g16,g10)
    c: Vertical(g32)
    c: Vertical(g28)
    c: Vertical(g15)
    c: Vertical(g11)
    c: Vertical(g8)
    c: Vertical(g2)
    c: Vertical(g13)
    c: Vertical(g30)
    c: Horizontal(g33)
    c: Horizontal(g27)
    c: Horizontal(g21)
    c: Horizontal(g17)
    c: Horizontal(g23)
    c: Horizontal(g19)
    c: Horizontal(g7)
    c: Horizontal(g3)
    c: Parallel(g4,g31)
    c: Parallel(g31,g14)
    c: Parallel(g14,g20)
    c: Parallel(g6,g12)
    c: Parallel(g12,g22)
    c: Parallel(g22,g29)
    c: Equal(g21,g22)
    c: Equal(g22,g29)
    c: Equal(g4,g31)
    c: Equal(g6,g12)
    c: Equal(g14,g20)
    c: Angle(g23,g22) = 0.785398
    c: Distance(g8,g2) = 8.13
    c: Distance(g27,g33) = 8.13
    c: Tangent(g33,g10)
    c: Tangent(g16,g27)
    c: Tangent(g2,g24)
    c: Tangent(g8,g18)
    c: Distance(g20,g14) = 4.32
    c: Distance(g12,g6) = 4.32
    c: Distance(g31,g4) = 4.32
    c: Distance(g22,g29) = 4.32
    c: Equal(g30,g13)
    c: Equal(g5,g21)
    c: Equal(g23,g19)
    c: Equal(g32,g28)
    c: Distance(g33,g33) = 4.32
    c: Symmetric(g5,g20,g-1)
    c: Symmetric(g4,g5,g-2)
    c: Equal(g5,g30)
    c: Coincident(g34,g-1)
    c: Diameter(g34) = 6.81
    c: Coincident(g35,g9)
    c: Coincident(g36,g35)
    c: Coincident(g37,g36)
    c: Horizontal(g37)
    c: Coincident(g38,g37)
    c: Coincident(g39,g38)
    c: Horizontal(g39)
    c: Coincident(g41,g40)
    c: Vertical(g44)
    c: Coincident(g45,g44)
    c: Coincident(g48,g47)
    c: Vertical(g48)
    c: Coincident(g49,g48)
    c: Vertical(g50)
    c: Horizontal(g51)
    c: Coincident(g52,g51)
    c: Vertical(g52)
    c: Coincident(g53,g52)
    c: Coincident(g55,g54)
    c: Coincident(g57,g56)
    c: Horizontal(g57)
    c: Coincident(g58,g57)
    c: Coincident(g59,g58)
    c: Horizontal(g59)
    c: Coincident(g61,g60)
    c: Coincident(g61,g17)
    c: Coincident(g63,g10)
    c: Coincident(g64,g16)
    c: Coincident(g65,g64)
    c: Coincident(g66,g65)
    c: Coincident(g67,g66)
    c: Coincident(g68,g67)
    c: Coincident(g68,g62)
    c: PointOnObject(g69,g-1)
    c: Coincident(g43,g42)
    c: Coincident(g43,g44)
    c: Coincident(g41,g42)
    c: Coincident(g39,g40)
    c: Coincident(g46,g47)
    c: Coincident(g46,g45)
    c: Coincident(g50,g51)
    c: Coincident(g49,g50)
    c: Coincident(g54,g53)
    c: Coincident(g56,g55)
    c: Coincident(g59,g60)
    c: Coincident(g62,g63)
    c: Equal(g34,g69)
    c: Equal(g39,g67)
    c: Equal(g67,g57)
    c: Equal(g57,g48)
    c: Equal(g48,g13)
    c: Equal(g38,g68)
    c: Equal(g68,g66)
    c: Equal(g66,g58)
    c: Equal(g58,g56)
    c: Equal(g56,g49)
    c: Equal(g49,g47)
    c: Equal(g47,g40)
    c: Equal(g40,g12)
    c: Equal(g10,g63)
    c: Equal(g16,g64)
    c: Equal(g64,g45)
    c: Equal(g45,g51)
    c: Equal(g51,g42)
    c: Equal(g42,g36)
    c: Equal(g36,g60)
    c: Equal(g60,g54)
    c: Parallel(g47,g40)
    c: Parallel(g38,g68)
    c: Parallel(g66,g58)
    c: Parallel(g49,g56)
    c: Parallel(g56,g68)
    c: Parallel(g40,g66)
    c: Horizontal(g35)
    c: Horizontal(g43)
    c: Horizontal(g45)
    c: Horizontal(g53)
    c: Horizontal(g61)
    c: Horizontal(g64)
    c: Horizontal(g63)
    c: Horizontal(g41)
    c: Vertical(g42)
    c: Vertical(g36)
    c: Vertical(g62)
    c: Vertical(g65)
    c: Vertical(g60)
    c: Vertical(g54)
    c: Vertical(g46)
    c: Horizontal(g55)
    c: Vertical(g67)
    c: Equal(g7,g37)
    c: Equal(g37,g41)
    c: Equal(g41,g46)
    c: Equal(g46,g55)
    c: Equal(g55,g59)
    c: Equal(g59,g65)
    c: Equal(g65,g62)
    c: Equal(g55,g50)
    c: Parallel(g40,g6)
    c: Distance(g9,g44) = 40
    c: DistanceX(g34,g69) = 40
    c: Equal(g35,g43)
    c: Equal(g43,g9)
    c: Equal(g44,g52)
    c: Equal(g53,g61)
    c: Equal(g61,g17)
FEATURE [PartDesign::Pad] Pad004
  Direction = (0,0,1)
  Length = 470
  Length2 = 10
  Profile = -> Sketch005
  ReferenceAxis = -> Sketch005 [N_Axis]
  Refine = true
  Suppressed = false
  Type = 0
FEATURE [PartDesign::Body] Body005  label="8040 extrusion @ 470"
  AllowCompound = false
  Group = -> [Sketch005,Pad004]
  Origin = -> Origin007
  Tip = -> Pad004
COMPONENT P25 — same part as P24; its construction recipe is shown at P24.
COMPONENT P26 — same part as P24; its construction recipe is shown at P24.
COMPONENT P27 — same part as P24; its construction recipe is shown at P24.
COMPONENT P28 — geometry summary ("corner gusset038"; no construction recipe available for this part):
  bounding box: 40.0 x 40.0 x 35.0 mm
  tessellated surface: 476 triangles
  volume: 10457 mm^3 (19% of its bounding box)
COMPONENT P29 — geometry summary ("corner gusset039"; no construction recipe available for this part):
  bounding box: 40.0 x 40.0 x 35.0 mm
  tessellated surface: 476 triangles
  volume: 10457 mm^3 (19% of its bounding box)
COMPONENT P30 — geometry summary ("corner gusset040"; no construction recipe available for this part):
  bounding box: 40.0 x 40.0 x 35.0 mm
  tessellated surface: 476 triangles
  volume: 10457 mm^3 (19% of its bounding box)
COMPONENT P31 — geometry summary ("corner gusset041"; no construction recipe available for this part):
  bounding box: 40.0 x 40.0 x 35.0 mm
  tessellated surface: 476 triangles
  volume: 10457 mm^3 (19% of its bounding box)
COMPONENT P32 — geometry summary ("corner gusset042"; no construction recipe available for this part):
  bounding box: 40.0 x 40.0 x 35.0 mm
  tessellated surface: 476 triangles
  volume: 10457 mm^3 (19% of its bounding box)
COMPONENT P33 — geometry summary ("corner gusset043"; no construction recipe available for this part):
  bounding box: 40.0 x 40.0 x 35.0 mm
  tessellated surface: 476 triangles
  volume: 10457 mm^3 (19% of its bounding box)
COMPONENT P34 — geometry summary ("corner gusset044"; no construction recipe available for this part):
  bounding box: 40.0 x 40.0 x 35.0 mm
  tessellated surface: 476 triangles
  volume: 10457 mm^3 (19% of its bounding box)
COMPONENT P35 — geometry summary ("corner gusset045"; no construction recipe available for this part):
  bounding box: 40.0 x 40.0 x 35.0 mm
  tessellated surface: 476 triangles
  volume: 10457 mm^3 (19% of its bounding box)
COMPONENT P36 — geometry summary ("corner gusset046"; no construction recipe available for this part):
  bounding box: 40.0 x 40.0 x 35.0 mm
  tessellated surface: 476 triangles
  volume: 10457 mm^3 (19% of its bounding box)
COMPONENT P37 — geometry summary ("corner gusset047"; no construction recipe available for this part):
  bounding box: 40.0 x 40.0 x 35.0 mm
  tessellated surface: 476 triangles
  volume: 10457 mm^3 (19% of its bounding box)
COMPONENT P38 — geometry summary ("corner gusset048"; no construction recipe available for this part):
  bounding box: 40.0 x 40.0 x 35.0 mm
  tessellated surface: 476 triangles
  volume: 10457 mm^3 (19% of its bounding box)
COMPONENT P39 — geometry summary ("corner gusset049"; no construction recipe available for this part):
  bounding box: 40.0 x 40.0 x 35.0 mm
  tessellated surface: 476 triangles
  volume: 10457 mm^3 (19% of its bounding box)
COMPONENT P40 — geometry summary ("corner gusset050"; no construction recipe available for this part):
  bounding box: 40.0 x 40.0 x 35.0 mm
  tessellated surface: 476 triangles
  volume: 10457 mm^3 (19% of its bounding box)
COMPONENT P41 — geometry summary ("corner gusset051"; no construction recipe available for this part):
  bounding box: 40.0 x 40.0 x 35.0 mm
  tessellated surface: 476 triangles
  volume: 10457 mm^3 (19% of its bounding box)
COMPONENT P42 — geometry summary ("corner gusset052"; no construction recipe available for this part):
  bounding box: 40.0 x 40.0 x 35.0 mm
  tessellated surface: 476 triangles
  volume: 10457 mm^3 (19% of its bounding box)
COMPONENT P43 — geometry summary ("corner gusset053"; no construction recipe available for this part):
  bounding box: 40.0 x 40.0 x 35.0 mm
  tessellated surface: 476 triangles
  volume: 10457 mm^3 (19% of its bounding box)
COMPONENT P44 — geometry summary ("corner gusset054"; no construction recipe available for this part):
  bounding box: 40.0 x 40.0 x 35.0 mm
  tessellated surface: 476 triangles
  volume: 10457 mm^3 (19% of its bounding box)
COMPONENT P45 — geometry summary ("corner gusset055"; no construction recipe available for this part):
  bounding box: 40.0 x 40.0 x 35.0 mm
  tessellated surface: 476 triangles
  volume: 10457 mm^3 (19% of its bounding box)
COMPONENT P46 — geometry summary ("corner gusset056"; no construction recipe available for this part):
  bounding box: 40.0 x 40.0 x 35.0 mm
  tessellated surface: 476 triangles
  volume: 10457 mm^3 (19% of its bounding box)
COMPONENT P47 — geometry summary ("corner gusset057"; no construction recipe available for this part):
  bounding box: 40.0 x 40.0 x 35.0 mm
  tessellated surface: 476 triangles
  volume: 10457 mm^3 (19% of its bounding box)
COMPONENT P48 — geometry summary ("corner gusset058"; no construction recipe available for this part):
  bounding box: 40.0 x 40.0 x 35.0 mm
  tessellated surface: 476 triangles
  volume: 10457 mm^3 (19% of its bounding box)
COMPONENT P49 — geometry summary ("corner gusset059"; no construction recipe available for this part):
  bounding box: 40.0 x 40.0 x 35.0 mm
  tessellated surface: 476 triangles
  volume: 10457 mm^3 (19% of its bounding box)
COMPONENT P50 — geometry summary ("corner gusset060"; no construction recipe available for this part):
  bounding box: 40.0 x 40.0 x 35.0 mm
  tessellated surface: 476 triangles
  volume: 10457 mm^3 (19% of its bounding box)
COMPONENT P51 — geometry summary ("corner gusset061"; no construction recipe available for this part):
  bounding box: 40.0 x 40.0 x 35.0 mm
  tessellated surface: 476 triangles
  volume: 10457 mm^3 (19% of its bounding box)
COMPONENT P52 — geometry summary ("corner gusset062"; no construction recipe available for this part):
  bounding box: 40.0 x 40.0 x 35.0 mm
  tessellated surface: 476 triangles
  volume: 10457 mm^3 (19% of its bounding box)
COMPONENT P53 — geometry summary ("corner gusset063"; no construction recipe available for this part):
  bounding box: 40.0 x 40.0 x 35.0 mm
  tessellated surface: 476 triangles
  volume: 10457 mm^3 (19% of its bounding box)
COMPONENT P54 — geometry summary ("corner gusset064"; no construction recipe available for this part):
  bounding box: 40.0 x 40.0 x 35.0 mm
  tessellated surface: 476 triangles
  volume: 10457 mm^3 (19% of its bounding box)
COMPONENT P55 — geometry summary ("corner gusset065"; no construction recipe available for this part):
  bounding box: 40.0 x 40.0 x 35.0 mm
  tessellated surface: 476 triangles
  volume: 10457 mm^3 (19% of its bounding box)
COMPONENT P56 — geometry summary ("corner gusset066"; no construction recipe available for this part):
  bounding box: 40.0 x 40.0 x 35.0 mm
  tessellated surface: 476 triangles
  volume: 10457 mm^3 (19% of its bounding box)
COMPONENT P57 — geometry summary ("corner gusset067"; no construction recipe available for this part):
  bounding box: 40.0 x 40.0 x 35.0 mm
  tessellated surface: 476 triangles
  volume: 10457 mm^3 (19% of its bounding box)
COMPONENT P58 — geometry summary ("corner gusset068"; no construction recipe available for this part):
  bounding box: 40.0 x 40.0 x 35.0 mm
  tessellated surface: 476 triangles
  volume: 10457 mm^3 (19% of its bounding box)
COMPONENT P59 — geometry summary ("corner gusset069"; no construction recipe available for this part):
  bounding box: 40.0 x 40.0 x 35.0 mm
  tessellated surface: 476 triangles
  volume: 10457 mm^3 (19% of its bounding box)
COMPONENT P60 — geometry summary ("corner gusset070"; no construction recipe available for this part):
  bounding box: 40.0 x 40.0 x 35.0 mm
  tessellated surface: 476 triangles
  volume: 10457 mm^3 (19% of its bounding box)
COMPONENT P61 — geometry summary ("corner gusset071"; no construction recipe available for this part):
  bounding box: 40.0 x 40.0 x 35.0 mm
  tessellated surface: 476 triangles
  volume: 10457 mm^3 (19% of its bounding box)
COMPONENT P62 — geometry summary ("corner gusset072"; no construction recipe available for this part):
  bounding box: 40.0 x 40.0 x 35.0 mm
  tessellated surface: 476 triangles
  volume: 10457 mm^3 (19% of its bounding box)
COMPONENT P63 — geometry summary ("corner gusset073"; no construction recipe available for this part):
  bounding box: 40.0 x 40.0 x 35.0 mm
  tessellated surface: 476 triangles
  volume: 10457 mm^3 (19% of its bounding box)
COMPONENT P64 — recipe-attached ("hgr carriage spacer001", modeled in this document).
Construction recipe (the document's own serialized feature program — sketch geometry with constraints, then the solid features built on it; lengths are millimeters unless a unit is written):

FEATURE [Sketcher::SketchObject] Sketch030
  ArcFitTolerance = 1e-06
  AttachmentSupport = -> [XY_Plane024]
  FullyConstrained = true
  MakeInternals = false
  MapMode = 5
  sketch-geometry (18):
    g0: LineSegment StartX=0 StartY=0 StartZ=0 EndX=50 EndY=0 EndZ=0
    g1: LineSegment StartX=50 StartY=0 StartZ=0 EndX=50 EndY=73 EndZ=0
    g2: LineSegment StartX=50 StartY=73 StartZ=0 EndX=0 EndY=73 EndZ=0
    g3: LineSegment StartX=0 StartY=73 StartZ=0 EndX=0 EndY=0 EndZ=0
    g4: Circle CenterX=9 CenterY=54.5 CenterZ=0 NormalX=0 NormalY=0 NormalZ=1 AngleXU=0 Radius=2.5
    g5: Circle CenterX=9 CenterY=18.5 CenterZ=0 NormalX=0 NormalY=0 NormalZ=1 AngleXU=0 Radius=2.5
    g6: Circle CenterX=41 CenterY=54.5 CenterZ=0 NormalX=0 NormalY=0 NormalZ=1 AngleXU=0 Radius=2.5
    g7: Circle CenterX=41 CenterY=18.5 CenterZ=0 NormalX=0 NormalY=0 NormalZ=1 AngleXU=0 Radius=2.5
    g8: LineSegment [constr] StartX=9 StartY=54.5 StartZ=0 EndX=41 EndY=54.5 EndZ=0
    g9: LineSegment [constr] StartX=9 StartY=18.5 StartZ=0 EndX=41 EndY=18.5 EndZ=0
    g10: LineSegment [constr] StartX=9 StartY=54.5 StartZ=0 EndX=9 EndY=18.5 EndZ=0
    g11: LineSegment [constr] StartX=41 StartY=54.5 StartZ=0 EndX=41 EndY=18.5 EndZ=0
    g12: GeomPoint X=25 Y=54.5 Z=0
    g13: GeomPoint X=41 Y=36.5 Z=0
    g14: GeomPoint X=9 Y=36.5 Z=0
    g15: GeomPoint X=25 Y=18.5 Z=0
    g16: LineSegment [constr] StartX=9 StartY=36.5 StartZ=0 EndX=41 EndY=36.5 EndZ=0
    g17: LineSegment [constr] StartX=25 StartY=54.5 StartZ=0 EndX=25 EndY=18.5 EndZ=0
  constraints (37):
    c: Coincident(g0,g1)
    c: Coincident(g1,g2)
    c: Coincident(g2,g3)
    c: Coincident(g3,g0)
    c: Horizontal(g0)
    c: Horizontal(g2)
    c: Vertical(g1)
    c: Vertical(g3)
    c: Coincident(g0,g-1)
    c: DistanceY(g1,g1) = 73
    c: DistanceX(g2,g2) = 50
    c: Equal(g4,g6)
    c: Equal(g6,g7)
    c: Equal(g7,g5)
    c: Coincident(g8,g4)
    c: Coincident(g8,g6)
    c: Horizontal(g8)
    c: Coincident(g9,g5)
    c: Coincident(g9,g7)
    c: Coincident(g10,g4)
    c: Coincident(g10,g5)
    c: Vertical(g10)
    c: Coincident(g11,g6)
    c: Coincident(g11,g7)
    c: Diameter(g6) = 5
    c: DistanceY(g11,g11) = 36
    c: Distance(g8,g8) = 32
    c: Symmetric(g8,g8,g12)
    c: Symmetric(g11,g11,g13)
    c: Symmetric(g10,g10,g14)
    c: Symmetric(g9,g9,g15)
    c: Coincident(g16,g14)
    c: Coincident(g16,g13)
    c: Coincident(g17,g12)
    c: Coincident(g17,g15)
    c: Symmetric(g1,g0,g16)
    c: Symmetric(g2,g1,g17)
FEATURE [PartDesign::Pad] Pad019
  Direction = (0,0,1)
  Length = 30
  Length2 = 10
  Profile = -> Sketch030
  ReferenceAxis = -> Sketch030 [N_Axis]
  Refine = true
  Suppressed = false
  Type = 0
FEATURE [PartDesign::Body] Body019  label="hgr carriage spacer"
  AllowCompound = false
  Group = -> [Sketch030,Pad019]
  Origin = -> Origin024
  Tip = -> Pad019
COMPONENT P65 — same part as P64; its construction recipe is shown at P64.
COMPONENT P66 — same part as P64; its construction recipe is shown at P64.
COMPONENT P67 — same part as P64; its construction recipe is shown at P64.
COMPONENT P68 — same part as P5; its construction recipe is shown at P5.
COMPONENT P69 — recipe-attached ("sfu1605x500mm001", modeled in this document).
Construction recipe (the document's own serialized feature program — sketch geometry with constraints, then the solid features built on it; lengths are millimeters unless a unit is written):

FEATURE [Sketcher::SketchObject] Sketch031
  ArcFitTolerance = 1e-06
  AttachmentSupport = -> [XY_Plane025]
  FullyConstrained = true
  MakeInternals = false
  MapMode = 5
  sketch-geometry (8):
    g0: LineSegment StartX=0 StartY=0 StartZ=0 EndX=500 EndY=0 EndZ=0
    g1: LineSegment StartX=0 StartY=0 StartZ=0 EndX=0 EndY=5 EndZ=0
    g2: LineSegment StartX=0 StartY=5 StartZ=0 EndX=54 EndY=5 EndZ=0
    g3: LineSegment StartX=54 StartY=5 StartZ=0 EndX=54 EndY=8 EndZ=0
    g4: LineSegment StartX=500 StartY=0 StartZ=0 EndX=500 EndY=5 EndZ=0
    g5: LineSegment StartX=500 StartY=5 StartZ=0 EndX=489 EndY=5 EndZ=0
    g6: LineSegment StartX=489 StartY=5 StartZ=0 EndX=489 EndY=8 EndZ=0
    g7: LineSegment StartX=489 StartY=8 StartZ=0 EndX=54 EndY=8 EndZ=0
  constraints (23):
    c: Coincident(g0,g-1)
    c: Horizontal(g0)
    c: DistanceX(g0,g0) = 500
    c: Coincident(g1,g0)
    c: PointOnObject(g1,g-2)
    c: Distance(g1,g1) = 5
    c: Coincident(g2,g1)
    c: Horizontal(g2)
    c: DistanceX(g2,g2) = 54
    c: Coincident(g3,g2)
    c: Vertical(g3)
    c: Distance(g3,g3) = 3
    c: Coincident(g4,g0)
    c: Vertical(g4)
    c: DistanceY(g4,g4) = 5
    c: Coincident(g5,g4)
    c: Horizontal(g5)
    c: DistanceX(g5,g5) = 11
    c: Coincident(g6,g5)
    c: Vertical(g6)
    c: DistanceY(g6,g6) = 3
    c: Coincident(g7,g6)
    c: Coincident(g7,g3)
FEATURE [PartDesign::Revolution] Revolution
  Angle = 360
  Angle2 = 60
  Axis = (1,0,0)
  Base = (0,0,0)
  Profile = -> Sketch031
  ReferenceAxis = -> Sketch031 [H_Axis]
  Refine = true
  Suppressed = false
  Type = 0
FEATURE [PartDesign::Body] Body020  label="sfu1605x500mm"
  AllowCompound = false
  Group = -> [Sketch031,Revolution]
  Origin = -> Origin025
  Tip = -> Revolution
PROVENANCE & LICENSES
A FreeCAD (.FCStd) document from a public repository crawl; recipes are the document's own serialized feature recipes (and, for linked parts, companion documents' recipes).
License: as declared in the source repository (recorded in the dataset sidecar).
